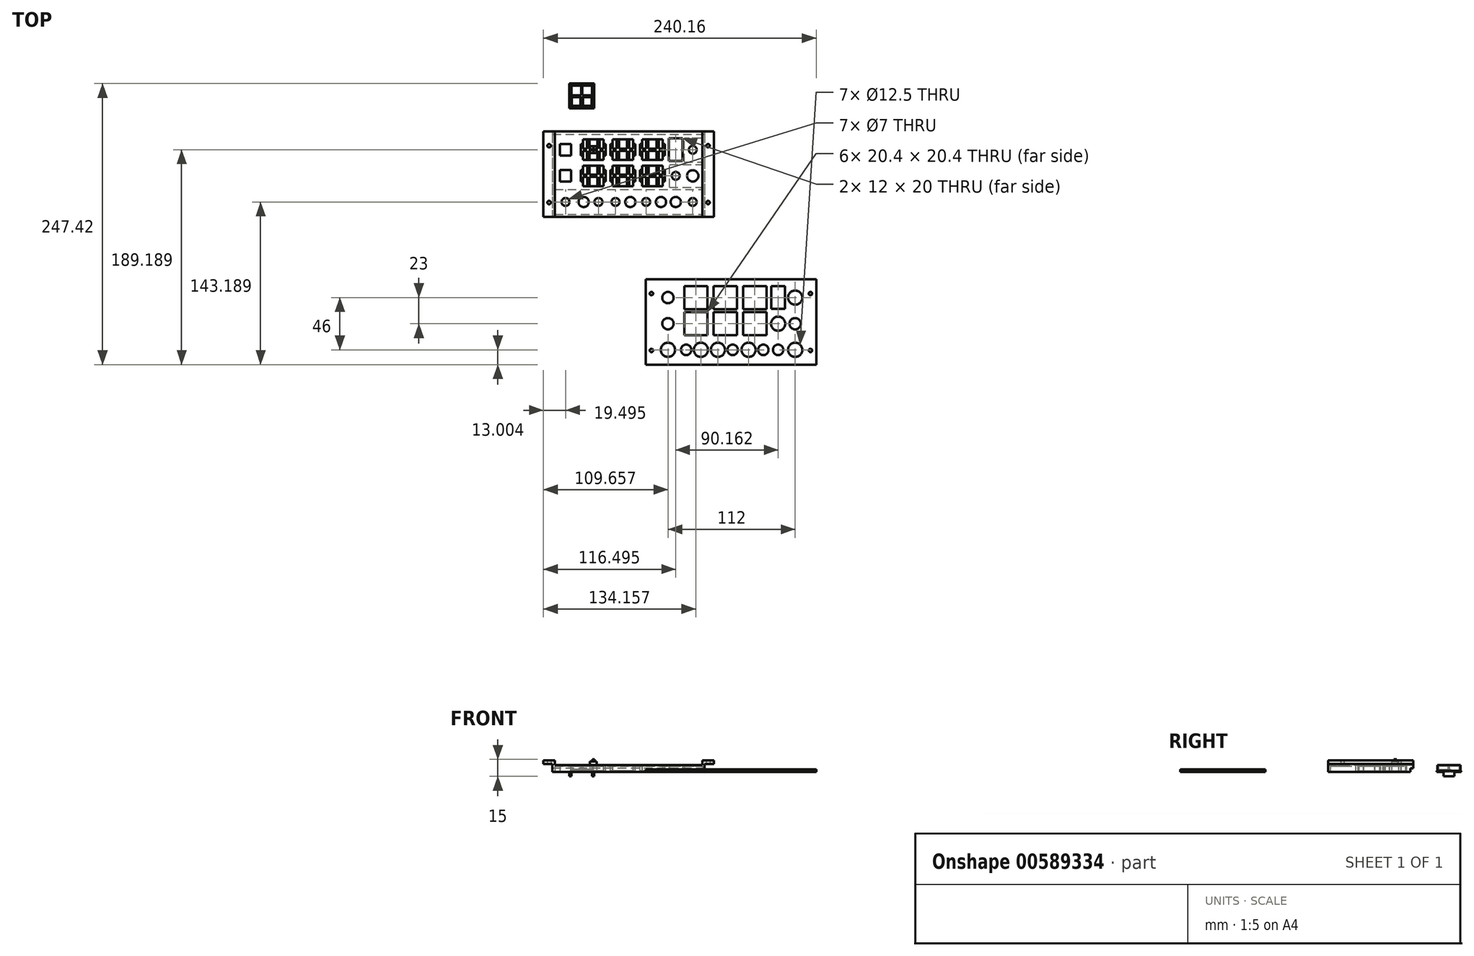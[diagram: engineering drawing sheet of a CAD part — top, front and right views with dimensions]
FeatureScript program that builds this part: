
annotation { "Feature Type Name" : "Feature", "Feature Type Description" : "" }
export const myFeature = defineFeature(function(context is Context, id is Id, definition is map)
    precondition{}
    {
        {
            var Q0;
            Q0=qCreatedBy(makeId("Top.planeOp"),FACE);
            var sketch = newSketch(context, id + "F0", { "sketchPlane" : qUnion([Q0])});
            skLineSegment(sketch, "E0.bottom", {"start": v(-5.5, -57.04) * mm, "end": v(-155.5, -57.04) * mm});
            skLineSegment(sketch, "E0.top", {"start": v(-5.5, 17.96) * mm, "end": v(-155.5, 17.96) * mm});
            skLineSegment(sketch, "E0.left", {"start": v(-5.5, -57.04) * mm, "end": v(-5.5, 17.96) * mm});
            skLineSegment(sketch, "E0.right", {"start": v(-155.5, -57.04) * mm, "end": v(-155.5, 17.96) * mm});
            skPoint(sketch, "E0.middle", {"position": v(-80.5, -19.54) * mm});
            skLineSegment(sketch, "E1.bottom", {"start": v(-101.5, -8.04) * mm, "end": v(-121.5, -8.04) * mm, "construction": true});
            skLineSegment(sketch, "E1.top", {"start": v(-101.5, 11.96) * mm, "end": v(-121.5, 11.96) * mm, "construction": true});
            skLineSegment(sketch, "E1.left", {"start": v(-101.5, -8.04) * mm, "end": v(-101.5, 11.96) * mm, "construction": true});
            skLineSegment(sketch, "E1.right", {"start": v(-121.5, -8.04) * mm, "end": v(-121.5, 11.96) * mm, "construction": true});
            skPoint(sketch, "E1.middle", {"position": v(-111.5, 1.96) * mm});
            skLineSegment(sketch, "E2.1.0.0", {"start": v(-95.5, -8.04) * mm, "end": v(-95.5, 11.96) * mm, "construction": true});
            skPoint(sketch, "E2.1.0.1", {"position": v(-85.5, 1.96) * mm});
            skLineSegment(sketch, "E2.1.0.2", {"start": v(-75.5, -8.04) * mm, "end": v(-95.5, -8.04) * mm, "construction": true});
            skLineSegment(sketch, "E2.1.0.3", {"start": v(-75.5, -8.04) * mm, "end": v(-75.5, 11.96) * mm, "construction": true});
            skLineSegment(sketch, "E2.1.0.4", {"start": v(-75.5, 11.96) * mm, "end": v(-95.5, 11.96) * mm, "construction": true});
            skLineSegment(sketch, "E2.2.0.0", {"start": v(-69.5, -8.04) * mm, "end": v(-69.5, 11.96) * mm, "construction": true});
            skPoint(sketch, "E2.2.0.1", {"position": v(-59.5, 1.96) * mm});
            skLineSegment(sketch, "E2.2.0.2", {"start": v(-49.5, -8.04) * mm, "end": v(-69.5, -8.04) * mm, "construction": true});
            skLineSegment(sketch, "E2.2.0.3", {"start": v(-49.5, -8.04) * mm, "end": v(-49.5, 11.96) * mm, "construction": true});
            skLineSegment(sketch, "E2.2.0.4", {"start": v(-49.5, 11.96) * mm, "end": v(-69.5, 11.96) * mm, "construction": true});
            skLineSegment(sketch, "E2.direction1", {"start": v(-121.5, -8.04) * mm, "end": v(-95.5, -8.04) * mm, "construction": true});
            skLineSegment(sketch, "E3.bottom", {"start": v(-101.5, -31.04) * mm, "end": v(-121.5, -31.04) * mm, "construction": true});
            skLineSegment(sketch, "E3.top", {"start": v(-101.5, -11.04) * mm, "end": v(-121.5, -11.04) * mm, "construction": true});
            skLineSegment(sketch, "E3.left", {"start": v(-101.5, -31.04) * mm, "end": v(-101.5, -11.04) * mm, "construction": true});
            skLineSegment(sketch, "E3.right", {"start": v(-121.5, -31.04) * mm, "end": v(-121.5, -11.04) * mm, "construction": true});
            skPoint(sketch, "E3.middle", {"position": v(-111.5, -21.04) * mm});
            skLineSegment(sketch, "E4.1.0.0", {"start": v(-75.5, -31.04) * mm, "end": v(-95.5, -31.04) * mm, "construction": true});
            skLineSegment(sketch, "E4.1.0.1", {"start": v(-75.5, -31.04) * mm, "end": v(-75.5, -11.04) * mm, "construction": true});
            skLineSegment(sketch, "E4.1.0.2", {"start": v(-95.5, -31.04) * mm, "end": v(-95.5, -11.04) * mm, "construction": true});
            skLineSegment(sketch, "E4.1.0.3", {"start": v(-75.5, -11.04) * mm, "end": v(-95.5, -11.04) * mm, "construction": true});
            skPoint(sketch, "E4.1.0.4", {"position": v(-85.5, -21.04) * mm});
            skLineSegment(sketch, "E4.2.0.0", {"start": v(-49.5, -31.04) * mm, "end": v(-69.5, -31.04) * mm, "construction": true});
            skLineSegment(sketch, "E4.2.0.1", {"start": v(-49.5, -31.04) * mm, "end": v(-49.5, -11.04) * mm, "construction": true});
            skLineSegment(sketch, "E4.2.0.2", {"start": v(-69.5, -31.04) * mm, "end": v(-69.5, -11.04) * mm, "construction": true});
            skLineSegment(sketch, "E4.2.0.3", {"start": v(-49.5, -11.04) * mm, "end": v(-69.5, -11.04) * mm, "construction": true});
            skPoint(sketch, "E4.2.0.4", {"position": v(-59.5, -21.04) * mm});
            skLineSegment(sketch, "E4.direction1", {"start": v(-121.5, -31.04) * mm, "end": v(-95.5, -31.04) * mm, "construction": true});
            skCircle(sketch, "E5", {"center": v(-136, -44.04) * mm, "radius": 3.5 * mm});
            skCircle(sketch, "E6", {"center": v(-107, -44.04) * mm, "radius": 3.5 * mm});
            skCircle(sketch, "E7", {"center": v(-92, -44.04) * mm, "radius": 3.5 * mm});
            skLineSegment(sketch, "E8.bottom", {"start": v(-155.5, 17.96) * mm, "end": v(-147.5, 17.96) * mm, "construction": true});
            skLineSegment(sketch, "E8.top", {"start": v(-155.5, -57.04) * mm, "end": v(-147.5, -57.04) * mm, "construction": true});
            skLineSegment(sketch, "E8.left", {"start": v(-155.5, 17.96) * mm, "end": v(-155.5, -57.04) * mm, "construction": true});
            skLineSegment(sketch, "E8.right", {"start": v(-147.5, 17.96) * mm, "end": v(-147.5, -57.04) * mm, "construction": true});
            skLineSegment(sketch, "E9.bottom", {"start": v(-5.5, -57.04) * mm, "end": v(-13.5, -57.04) * mm, "construction": true});
            skLineSegment(sketch, "E9.top", {"start": v(-5.5, 17.96) * mm, "end": v(-13.5, 17.96) * mm, "construction": true});
            skLineSegment(sketch, "E9.left", {"start": v(-5.5, -57.04) * mm, "end": v(-5.5, 17.96) * mm, "construction": true});
            skLineSegment(sketch, "E9.right", {"start": v(-13.5, -57.04) * mm, "end": v(-13.5, 17.96) * mm, "construction": true});
            skCircle(sketch, "E10", {"center": v(-120, -44.04) * mm, "radius": 4.5 * mm});
            skCircle(sketch, "E11", {"center": v(-79, -44.04) * mm, "radius": 4.5 * mm});
            skCircle(sketch, "E12", {"center": v(-65, -44.04) * mm, "radius": 3.5 * mm});
            skCircle(sketch, "E13", {"center": v(-52, -44.04) * mm, "radius": 4.5 * mm});
            skCircle(sketch, "E14", {"center": v(-39, -44.04) * mm, "radius": 4.5 * mm});
            skCircle(sketch, "E15", {"center": v(-24, -44.04) * mm, "radius": 3.5 * mm});
            skCircle(sketch, "E16", {"center": v(-39, -21.04) * mm, "radius": 3.5 * mm});
            skLineSegment(sketch, "E17.bottom", {"start": v(-33, -8.04) * mm, "end": v(-45, -8.04) * mm});
            skLineSegment(sketch, "E17.top", {"start": v(-33, 11.96) * mm, "end": v(-45, 11.96) * mm});
            skLineSegment(sketch, "E17.left", {"start": v(-33, -8.04) * mm, "end": v(-33, 11.96) * mm});
            skLineSegment(sketch, "E17.right", {"start": v(-45, -8.04) * mm, "end": v(-45, 11.96) * mm});
            skPoint(sketch, "E17.middle", {"position": v(-39, 1.96) * mm});
            skCircle(sketch, "E18", {"center": v(-24, 1.96) * mm, "radius": 3.5 * mm});
            skCircle(sketch, "E19", {"center": v(-24, -21.04) * mm, "radius": 5 * mm});
            skPoint(sketch, "E20.centerSnap0", {"position": v(-121.5, -21.04) * mm});
            skLineSegment(sketch, "E21.bottom", {"start": v(-102.5, -7.04) * mm, "end": v(-120.5, -7.04) * mm});
            skLineSegment(sketch, "E21.top", {"start": v(-102.5, 10.96) * mm, "end": v(-120.5, 10.96) * mm});
            skLineSegment(sketch, "E21.left", {"start": v(-102.5, -7.04) * mm, "end": v(-102.5, 10.96) * mm});
            skLineSegment(sketch, "E21.right", {"start": v(-120.5, -7.04) * mm, "end": v(-120.5, 10.96) * mm});
            skLineSegment(sketch, "E22.bottom", {"start": v(-102.5, -30.04) * mm, "end": v(-120.5, -30.04) * mm});
            skLineSegment(sketch, "E22.top", {"start": v(-102.5, -12.04) * mm, "end": v(-120.5, -12.04) * mm});
            skLineSegment(sketch, "E22.left", {"start": v(-102.5, -30.04) * mm, "end": v(-102.5, -12.04) * mm});
            skLineSegment(sketch, "E22.right", {"start": v(-120.5, -30.04) * mm, "end": v(-120.5, -12.04) * mm});
            skLineSegment(sketch, "E23.bottom", {"start": v(-102.5, 0.96) * mm, "end": v(-106, 0.96) * mm});
            skLineSegment(sketch, "E23.top", {"start": v(-102.5, 2.96) * mm, "end": v(-106, 2.96) * mm});
            skLineSegment(sketch, "E23.left", {"start": v(-102.5, 0.96) * mm, "end": v(-102.5, 2.96) * mm});
            skLineSegment(sketch, "E23.right", {"start": v(-120.5, 0.96) * mm, "end": v(-120.5, 2.96) * mm});
            skLineSegment(sketch, "E24.bottom", {"start": v(-115, -7.04) * mm, "end": v(-117, -7.04) * mm});
            skLineSegment(sketch, "E24.top", {"start": v(-115, 10.96) * mm, "end": v(-117, 10.96) * mm});
            skLineSegment(sketch, "E24.left", {"start": v(-115, -7.04) * mm, "end": v(-115, 0.96) * mm});
            skLineSegment(sketch, "E24.right", {"start": v(-117, -7.04) * mm, "end": v(-117, 0.96) * mm});
            skPoint(sketch, "E24.middle", {"position": v(-116, 1.96) * mm});
            skLineSegment(sketch, "E25.bottom", {"start": v(-106, -7.04) * mm, "end": v(-108, -7.04) * mm});
            skLineSegment(sketch, "E25.top", {"start": v(-106, 10.96) * mm, "end": v(-108, 10.96) * mm});
            skLineSegment(sketch, "E25.left", {"start": v(-106, -7.04) * mm, "end": v(-106, 0.96) * mm});
            skLineSegment(sketch, "E25.right", {"start": v(-108, -7.04) * mm, "end": v(-108, 0.96) * mm});
            skPoint(sketch, "E25.middle", {"position": v(-107, 1.96) * mm});
            skLineSegment(sketch, "E26.trimOffspring", {"start": v(-117, 2.96) * mm, "end": v(-117, 10.96) * mm});
            skLineSegment(sketch, "E27.trimOffspring", {"start": v(-117, 2.96) * mm, "end": v(-120.5, 2.96) * mm});
            skLineSegment(sketch, "E28.trimOffspring", {"start": v(-115, 2.96) * mm, "end": v(-115, 10.96) * mm});
            skLineSegment(sketch, "E29.trimOffspring", {"start": v(-117, 0.96) * mm, "end": v(-120.5, 0.96) * mm});
            skLineSegment(sketch, "E30.trimOffspring", {"start": v(-108, 2.96) * mm, "end": v(-108, 10.96) * mm});
            skLineSegment(sketch, "E31.trimOffspring", {"start": v(-108, 2.96) * mm, "end": v(-115, 2.96) * mm});
            skLineSegment(sketch, "E32.trimOffspring", {"start": v(-106, 2.96) * mm, "end": v(-106, 10.96) * mm});
            skLineSegment(sketch, "E33.trimOffspring", {"start": v(-108, 0.96) * mm, "end": v(-115, 0.96) * mm});
            skLineSegment(sketch, "E34.bottom", {"start": v(-132.5, -50.54) * mm, "end": v(-139.5, -50.54) * mm, "construction": true});
            skLineSegment(sketch, "E34.top", {"start": v(-132.5, -37.54) * mm, "end": v(-139.5, -37.54) * mm, "construction": true});
            skLineSegment(sketch, "E34.left", {"start": v(-132.5, -50.54) * mm, "end": v(-132.5, -37.54) * mm, "construction": true});
            skLineSegment(sketch, "E34.right", {"start": v(-139.5, -50.54) * mm, "end": v(-139.5, -37.54) * mm, "construction": true});
            skLineSegment(sketch, "E35.bottom", {"start": v(-102.5, -22.04) * mm, "end": v(-105.98, -22.04) * mm});
            skLineSegment(sketch, "E35.top", {"start": v(-102.5, -20.04) * mm, "end": v(-105.98, -20.04) * mm});
            skLineSegment(sketch, "E35.left", {"start": v(-102.5, -22.04) * mm, "end": v(-102.5, -20.04) * mm});
            skLineSegment(sketch, "E35.right", {"start": v(-120.5, -22.04) * mm, "end": v(-120.5, -20.04) * mm});
            skLineSegment(sketch, "E36.bottom", {"start": v(-114.98, -30.04) * mm, "end": v(-116.98, -30.04) * mm});
            skLineSegment(sketch, "E36.top", {"start": v(-114.98, -12.04) * mm, "end": v(-116.98, -12.04) * mm});
            skLineSegment(sketch, "E36.left", {"start": v(-114.98, -30.04) * mm, "end": v(-114.98, -22.04) * mm});
            skLineSegment(sketch, "E36.right", {"start": v(-116.98, -30.04) * mm, "end": v(-116.98, -22.04) * mm});
            skPoint(sketch, "E36.middle", {"position": v(-115.98, -21.04) * mm});
            skLineSegment(sketch, "E37.bottom", {"start": v(-105.98, -30.04) * mm, "end": v(-107.98, -30.04) * mm});
            skLineSegment(sketch, "E37.top", {"start": v(-105.98, -12.04) * mm, "end": v(-107.98, -12.04) * mm});
            skLineSegment(sketch, "E37.left", {"start": v(-105.98, -30.04) * mm, "end": v(-105.98, -22.04) * mm});
            skLineSegment(sketch, "E37.right", {"start": v(-107.98, -30.04) * mm, "end": v(-107.98, -22.04) * mm});
            skPoint(sketch, "E37.middle", {"position": v(-106.98, -21.04) * mm});
            skLineSegment(sketch, "E38.trimOffspring", {"start": v(-116.98, -20.04) * mm, "end": v(-116.98, -12.04) * mm});
            skLineSegment(sketch, "E39.trimOffspring", {"start": v(-116.98, -20.04) * mm, "end": v(-120.5, -20.04) * mm});
            skLineSegment(sketch, "E40.trimOffspring", {"start": v(-114.98, -20.04) * mm, "end": v(-114.98, -12.04) * mm});
            skLineSegment(sketch, "E41.trimOffspring", {"start": v(-116.98, -22.04) * mm, "end": v(-120.5, -22.04) * mm});
            skLineSegment(sketch, "E42.trimOffspring", {"start": v(-107.98, -20.04) * mm, "end": v(-107.98, -12.04) * mm});
            skLineSegment(sketch, "E43.trimOffspring", {"start": v(-107.98, -20.04) * mm, "end": v(-114.98, -20.04) * mm});
            skLineSegment(sketch, "E44.trimOffspring", {"start": v(-105.98, -20.04) * mm, "end": v(-105.98, -12.04) * mm});
            skLineSegment(sketch, "E45.trimOffspring", {"start": v(-107.98, -22.04) * mm, "end": v(-114.98, -22.04) * mm});
            skLineSegment(sketch, "E46.bottom", {"start": v(-131, -3.04) * mm, "end": v(-141, -3.04) * mm});
            skLineSegment(sketch, "E46.top", {"start": v(-131, 6.96) * mm, "end": v(-141, 6.96) * mm});
            skLineSegment(sketch, "E46.left", {"start": v(-131, -3.04) * mm, "end": v(-131, 6.96) * mm});
            skLineSegment(sketch, "E46.right", {"start": v(-141, -3.04) * mm, "end": v(-141, 6.96) * mm});
            skPoint(sketch, "E46.middle", {"position": v(-136, 1.96) * mm});
            skLineSegment(sketch, "E47.bottom", {"start": v(-131, -26.04) * mm, "end": v(-141, -26.04) * mm});
            skLineSegment(sketch, "E47.top", {"start": v(-131, -16.04) * mm, "end": v(-141, -16.04) * mm});
            skLineSegment(sketch, "E47.left", {"start": v(-131, -26.04) * mm, "end": v(-131, -16.04) * mm});
            skLineSegment(sketch, "E47.right", {"start": v(-141, -26.04) * mm, "end": v(-141, -16.04) * mm});
            skPoint(sketch, "E47.middle", {"position": v(-136, -21.04) * mm});
            skLineSegment(sketch, "E48.1.0.0", {"start": v(-91, 2.96) * mm, "end": v(-91, 10.96) * mm});
            skLineSegment(sketch, "E48.1.0.2", {"start": v(-76.5, -7.04) * mm, "end": v(-76.5, 10.96) * mm});
            skLineSegment(sketch, "E48.1.0.3", {"start": v(-80, -7.04) * mm, "end": v(-80, 0.96) * mm});
            skPoint(sketch, "E48.1.0.4", {"position": v(-90, 1.96) * mm});
            skLineSegment(sketch, "E48.1.0.5", {"start": v(-82, 2.96) * mm, "end": v(-82, 10.96) * mm});
            skLineSegment(sketch, "E48.1.0.6", {"start": v(-80, 2.96) * mm, "end": v(-80, 10.96) * mm});
            skLineSegment(sketch, "E48.1.0.7", {"start": v(-82, 2.96) * mm, "end": v(-89, 2.96) * mm});
            skLineSegment(sketch, "E48.1.0.8", {"start": v(-76.5, 2.96) * mm, "end": v(-80, 2.96) * mm});
            skLineSegment(sketch, "E48.1.0.9", {"start": v(-76.5, 0.96) * mm, "end": v(-80, 0.96) * mm});
            skLineSegment(sketch, "E48.1.0.10", {"start": v(-80, 10.96) * mm, "end": v(-82, 10.96) * mm});
            skPoint(sketch, "E48.1.0.11", {"position": v(-81, 1.96) * mm});
            skLineSegment(sketch, "E48.1.0.12", {"start": v(-91, 2.96) * mm, "end": v(-94.5, 2.96) * mm});
            skLineSegment(sketch, "E48.1.0.13", {"start": v(-91, 0.96) * mm, "end": v(-94.5, 0.96) * mm});
            skLineSegment(sketch, "E48.1.0.14", {"start": v(-89, 2.96) * mm, "end": v(-89, 10.96) * mm});
            skLineSegment(sketch, "E48.1.0.15", {"start": v(-76.5, 10.96) * mm, "end": v(-94.5, 10.96) * mm});
            skLineSegment(sketch, "E48.1.0.16", {"start": v(-91, -7.04) * mm, "end": v(-91, 0.96) * mm});
            skLineSegment(sketch, "E48.1.0.17", {"start": v(-76.5, -7.04) * mm, "end": v(-94.5, -7.04) * mm});
            skLineSegment(sketch, "E48.1.0.18", {"start": v(-89, -7.04) * mm, "end": v(-89, 0.96) * mm});
            skLineSegment(sketch, "E48.1.0.19", {"start": v(-82, -7.04) * mm, "end": v(-82, 0.96) * mm});
            skLineSegment(sketch, "E48.1.0.20", {"start": v(-94.5, -7.04) * mm, "end": v(-94.5, 10.96) * mm});
            skLineSegment(sketch, "E48.1.0.21", {"start": v(-82, 0.96) * mm, "end": v(-89, 0.96) * mm});
            skLineSegment(sketch, "E48.1.0.22", {"start": v(-80, -7.04) * mm, "end": v(-82, -7.04) * mm});
            skLineSegment(sketch, "E48.1.0.23", {"start": v(-76.5, 0.96) * mm, "end": v(-76.5, 2.96) * mm});
            skLineSegment(sketch, "E48.1.0.24", {"start": v(-89, -7.04) * mm, "end": v(-91, -7.04) * mm});
            skLineSegment(sketch, "E48.1.0.25", {"start": v(-94.5, 0.96) * mm, "end": v(-94.5, 2.96) * mm});
            skLineSegment(sketch, "E48.1.0.27", {"start": v(-89, 10.96) * mm, "end": v(-91, 10.96) * mm});
            skLineSegment(sketch, "E48.2.0.0", {"start": v(-65, 2.96) * mm, "end": v(-65, 10.96) * mm});
            skLineSegment(sketch, "E48.2.0.2", {"start": v(-50.5, -7.04) * mm, "end": v(-50.5, 10.96) * mm});
            skLineSegment(sketch, "E48.2.0.3", {"start": v(-54, -7.04) * mm, "end": v(-54, 0.96) * mm});
            skPoint(sketch, "E48.2.0.4", {"position": v(-64, 1.96) * mm});
            skLineSegment(sketch, "E48.2.0.5", {"start": v(-56, 2.96) * mm, "end": v(-56, 10.96) * mm});
            skLineSegment(sketch, "E48.2.0.6", {"start": v(-54, 2.96) * mm, "end": v(-54, 10.96) * mm});
            skLineSegment(sketch, "E48.2.0.7", {"start": v(-56, 2.96) * mm, "end": v(-63, 2.96) * mm});
            skLineSegment(sketch, "E48.2.0.8", {"start": v(-50.5, 2.96) * mm, "end": v(-54, 2.96) * mm});
            skLineSegment(sketch, "E48.2.0.9", {"start": v(-50.5, 0.96) * mm, "end": v(-54, 0.96) * mm});
            skLineSegment(sketch, "E48.2.0.10", {"start": v(-54, 10.96) * mm, "end": v(-56, 10.96) * mm});
            skPoint(sketch, "E48.2.0.11", {"position": v(-55, 1.96) * mm});
            skLineSegment(sketch, "E48.2.0.12", {"start": v(-65, 2.96) * mm, "end": v(-68.5, 2.96) * mm});
            skLineSegment(sketch, "E48.2.0.13", {"start": v(-65, 0.96) * mm, "end": v(-68.5, 0.96) * mm});
            skLineSegment(sketch, "E48.2.0.14", {"start": v(-63, 2.96) * mm, "end": v(-63, 10.96) * mm});
            skLineSegment(sketch, "E48.2.0.15", {"start": v(-50.5, 10.96) * mm, "end": v(-68.5, 10.96) * mm});
            skLineSegment(sketch, "E48.2.0.16", {"start": v(-65, -7.04) * mm, "end": v(-65, 0.96) * mm});
            skLineSegment(sketch, "E48.2.0.17", {"start": v(-50.5, -7.04) * mm, "end": v(-68.5, -7.04) * mm});
            skLineSegment(sketch, "E48.2.0.18", {"start": v(-63, -7.04) * mm, "end": v(-63, 0.96) * mm});
            skLineSegment(sketch, "E48.2.0.19", {"start": v(-56, -7.04) * mm, "end": v(-56, 0.96) * mm});
            skLineSegment(sketch, "E48.2.0.20", {"start": v(-68.5, -7.04) * mm, "end": v(-68.5, 10.96) * mm});
            skLineSegment(sketch, "E48.2.0.21", {"start": v(-56, 0.96) * mm, "end": v(-63, 0.96) * mm});
            skLineSegment(sketch, "E48.2.0.22", {"start": v(-54, -7.04) * mm, "end": v(-56, -7.04) * mm});
            skLineSegment(sketch, "E48.2.0.23", {"start": v(-50.5, 0.96) * mm, "end": v(-50.5, 2.96) * mm});
            skLineSegment(sketch, "E48.2.0.24", {"start": v(-63, -7.04) * mm, "end": v(-65, -7.04) * mm});
            skLineSegment(sketch, "E48.2.0.25", {"start": v(-68.5, 0.96) * mm, "end": v(-68.5, 2.96) * mm});
            skLineSegment(sketch, "E48.2.0.27", {"start": v(-63, 10.96) * mm, "end": v(-65, 10.96) * mm});
            skLineSegment(sketch, "E48.direction1", {"start": v(-120.5, -7.04) * mm, "end": v(-94.5, -7.04) * mm, "construction": true});
            skLineSegment(sketch, "E49.1.0.0", {"start": v(-76.5, -20.04) * mm, "end": v(-79.98, -20.04) * mm});
            skLineSegment(sketch, "E49.1.0.1", {"start": v(-88.98, -20.04) * mm, "end": v(-88.98, -12.04) * mm});
            skLineSegment(sketch, "E49.1.0.2", {"start": v(-81.98, -30.04) * mm, "end": v(-81.98, -22.04) * mm});
            skLineSegment(sketch, "E49.1.0.3", {"start": v(-94.5, -30.04) * mm, "end": v(-94.5, -12.04) * mm});
            skLineSegment(sketch, "E49.1.0.4", {"start": v(-90.98, -30.04) * mm, "end": v(-90.98, -22.04) * mm});
            skLineSegment(sketch, "E49.1.0.5", {"start": v(-76.5, -30.04) * mm, "end": v(-76.5, -12.04) * mm});
            skLineSegment(sketch, "E49.1.0.6", {"start": v(-81.98, -22.04) * mm, "end": v(-88.98, -22.04) * mm});
            skLineSegment(sketch, "E49.1.0.7", {"start": v(-88.98, -30.04) * mm, "end": v(-88.98, -22.04) * mm});
            skLineSegment(sketch, "E49.1.0.9", {"start": v(-79.98, -20.04) * mm, "end": v(-79.98, -12.04) * mm});
            skLineSegment(sketch, "E49.1.0.10", {"start": v(-76.5, -22.04) * mm, "end": v(-79.98, -22.04) * mm});
            skPoint(sketch, "E49.1.0.11", {"position": v(-80.98, -21.04) * mm});
            skLineSegment(sketch, "E49.1.0.12", {"start": v(-90.98, -22.04) * mm, "end": v(-94.5, -22.04) * mm});
            skLineSegment(sketch, "E49.1.0.14", {"start": v(-81.98, -20.04) * mm, "end": v(-88.98, -20.04) * mm});
            skPoint(sketch, "E49.1.0.15", {"position": v(-89.98, -21.04) * mm});
            skLineSegment(sketch, "E49.1.0.16", {"start": v(-79.98, -30.04) * mm, "end": v(-79.98, -22.04) * mm});
            skLineSegment(sketch, "E49.1.0.17", {"start": v(-76.5, -30.04) * mm, "end": v(-94.5, -30.04) * mm});
            skLineSegment(sketch, "E49.1.0.18", {"start": v(-90.98, -20.04) * mm, "end": v(-90.98, -12.04) * mm});
            skLineSegment(sketch, "E49.1.0.19", {"start": v(-81.98, -20.04) * mm, "end": v(-81.98, -12.04) * mm});
            skLineSegment(sketch, "E49.1.0.20", {"start": v(-90.98, -20.04) * mm, "end": v(-94.5, -20.04) * mm});
            skLineSegment(sketch, "E49.1.0.21", {"start": v(-76.5, -12.04) * mm, "end": v(-94.5, -12.04) * mm});
            skLineSegment(sketch, "E49.1.0.22", {"start": v(-88.98, -12.04) * mm, "end": v(-90.98, -12.04) * mm});
            skLineSegment(sketch, "E49.1.0.23", {"start": v(-76.5, -22.04) * mm, "end": v(-76.5, -20.04) * mm});
            skLineSegment(sketch, "E49.1.0.24", {"start": v(-94.5, -22.04) * mm, "end": v(-94.5, -20.04) * mm});
            skLineSegment(sketch, "E49.1.0.26", {"start": v(-94.5, -30.04) * mm, "end": v(-94.5, -12.04) * mm});
            skLineSegment(sketch, "E49.1.0.27", {"start": v(-79.98, -12.04) * mm, "end": v(-81.98, -12.04) * mm});
            skLineSegment(sketch, "E49.1.0.28", {"start": v(-76.5, -30.04) * mm, "end": v(-94.5, -30.04) * mm});
            skLineSegment(sketch, "E49.1.0.29", {"start": v(-76.5, -12.04) * mm, "end": v(-94.5, -12.04) * mm});
            skLineSegment(sketch, "E49.1.0.30", {"start": v(-76.5, -30.04) * mm, "end": v(-76.5, -12.04) * mm});
            skLineSegment(sketch, "E49.1.0.31", {"start": v(-88.98, -30.04) * mm, "end": v(-90.98, -30.04) * mm});
            skLineSegment(sketch, "E49.1.0.32", {"start": v(-79.98, -30.04) * mm, "end": v(-81.98, -30.04) * mm});
            skLineSegment(sketch, "E49.2.0.0", {"start": v(-50.5, -20.04) * mm, "end": v(-53.98, -20.04) * mm});
            skLineSegment(sketch, "E49.2.0.1", {"start": v(-62.98, -20.04) * mm, "end": v(-62.98, -12.04) * mm});
            skLineSegment(sketch, "E49.2.0.2", {"start": v(-55.98, -30.04) * mm, "end": v(-55.98, -22.04) * mm});
            skLineSegment(sketch, "E49.2.0.3", {"start": v(-68.5, -30.04) * mm, "end": v(-68.5, -12.04) * mm});
            skLineSegment(sketch, "E49.2.0.4", {"start": v(-64.98, -30.04) * mm, "end": v(-64.98, -22.04) * mm});
            skLineSegment(sketch, "E49.2.0.5", {"start": v(-50.5, -30.04) * mm, "end": v(-50.5, -12.04) * mm});
            skLineSegment(sketch, "E49.2.0.6", {"start": v(-55.98, -22.04) * mm, "end": v(-62.98, -22.04) * mm});
            skLineSegment(sketch, "E49.2.0.7", {"start": v(-62.98, -30.04) * mm, "end": v(-62.98, -22.04) * mm});
            skLineSegment(sketch, "E49.2.0.9", {"start": v(-53.98, -20.04) * mm, "end": v(-53.98, -12.04) * mm});
            skLineSegment(sketch, "E49.2.0.10", {"start": v(-50.5, -22.04) * mm, "end": v(-53.98, -22.04) * mm});
            skPoint(sketch, "E49.2.0.11", {"position": v(-54.98, -21.04) * mm});
            skLineSegment(sketch, "E49.2.0.12", {"start": v(-64.98, -22.04) * mm, "end": v(-68.5, -22.04) * mm});
            skLineSegment(sketch, "E49.2.0.14", {"start": v(-55.98, -20.04) * mm, "end": v(-62.98, -20.04) * mm});
            skPoint(sketch, "E49.2.0.15", {"position": v(-63.98, -21.04) * mm});
            skLineSegment(sketch, "E49.2.0.16", {"start": v(-53.98, -30.04) * mm, "end": v(-53.98, -22.04) * mm});
            skLineSegment(sketch, "E49.2.0.17", {"start": v(-50.5, -30.04) * mm, "end": v(-68.5, -30.04) * mm});
            skLineSegment(sketch, "E49.2.0.18", {"start": v(-64.98, -20.04) * mm, "end": v(-64.98, -12.04) * mm});
            skLineSegment(sketch, "E49.2.0.19", {"start": v(-55.98, -20.04) * mm, "end": v(-55.98, -12.04) * mm});
            skLineSegment(sketch, "E49.2.0.20", {"start": v(-64.98, -20.04) * mm, "end": v(-68.5, -20.04) * mm});
            skLineSegment(sketch, "E49.2.0.21", {"start": v(-50.5, -12.04) * mm, "end": v(-68.5, -12.04) * mm});
            skLineSegment(sketch, "E49.2.0.22", {"start": v(-62.98, -12.04) * mm, "end": v(-64.98, -12.04) * mm});
            skLineSegment(sketch, "E49.2.0.23", {"start": v(-50.5, -22.04) * mm, "end": v(-50.5, -20.04) * mm});
            skLineSegment(sketch, "E49.2.0.24", {"start": v(-68.5, -22.04) * mm, "end": v(-68.5, -20.04) * mm});
            skLineSegment(sketch, "E49.2.0.26", {"start": v(-68.5, -30.04) * mm, "end": v(-68.5, -12.04) * mm});
            skLineSegment(sketch, "E49.2.0.27", {"start": v(-53.98, -12.04) * mm, "end": v(-55.98, -12.04) * mm});
            skLineSegment(sketch, "E49.2.0.28", {"start": v(-50.5, -30.04) * mm, "end": v(-68.5, -30.04) * mm});
            skLineSegment(sketch, "E49.2.0.29", {"start": v(-50.5, -12.04) * mm, "end": v(-68.5, -12.04) * mm});
            skLineSegment(sketch, "E49.2.0.30", {"start": v(-50.5, -30.04) * mm, "end": v(-50.5, -12.04) * mm});
            skLineSegment(sketch, "E49.2.0.31", {"start": v(-62.98, -30.04) * mm, "end": v(-64.98, -30.04) * mm});
            skLineSegment(sketch, "E49.2.0.32", {"start": v(-53.98, -30.04) * mm, "end": v(-55.98, -30.04) * mm});
            skLineSegment(sketch, "E49.direction1", {"start": v(-120.5, -30.04) * mm, "end": v(-94.5, -30.04) * mm, "construction": true});
            skLineSegment(sketch, "E50.bottom", {"start": v(-135, -3.04) * mm, "end": v(-137, -3.04) * mm});
            skLineSegment(sketch, "E50.top", {"start": v(-135, 6.96) * mm, "end": v(-137, 6.96) * mm});
            skLineSegment(sketch, "E50.left", {"start": v(-135, -3.04) * mm, "end": v(-135, 6.96) * mm});
            skLineSegment(sketch, "E50.right", {"start": v(-137, -3.04) * mm, "end": v(-137, 6.96) * mm});
            skLineSegment(sketch, "E51.bottom", {"start": v(-135, -26.04) * mm, "end": v(-137, -26.04) * mm});
            skLineSegment(sketch, "E51.top", {"start": v(-135, -16.04) * mm, "end": v(-137, -16.04) * mm});
            skLineSegment(sketch, "E51.left", {"start": v(-135, -26.04) * mm, "end": v(-135, -16.04) * mm});
            skLineSegment(sketch, "E51.right", {"start": v(-137, -26.04) * mm, "end": v(-137, -16.04) * mm});
            skCircle(sketch, "E52", {"center": v(-150.5, 5.46) * mm, "radius": 1.5 * mm});
            skPoint(sketch, "E52.centerSnap0", {"position": v(-151.5, 17.96) * mm});
            skCircle(sketch, "E53", {"center": v(-150.5, -44.54) * mm, "radius": 1.5 * mm});
            skCircle(sketch, "E54", {"center": v(-10.5, 5.46) * mm, "radius": 1.5 * mm});
            skCircle(sketch, "E55", {"center": v(-10.5, -44.54) * mm, "radius": 1.5 * mm});
            skSolve(sketch);
        }
        {
            var Q0;
            Q0=qCreatedBy(makeId("Top.planeOp"),FACE);
            var sketch = newSketch(context, id + "F1", { "sketchPlane" : qUnion([Q0])});
            skLineSegment(sketch, "E56.bottom", {"start": v(84.66, -187.23) * mm, "end": v(-65.34, -187.23) * mm});
            skLineSegment(sketch, "E56.top", {"start": v(84.66, -112.23) * mm, "end": v(-65.34, -112.23) * mm});
            skLineSegment(sketch, "E56.left", {"start": v(84.66, -187.23) * mm, "end": v(84.66, -112.23) * mm});
            skLineSegment(sketch, "E56.right", {"start": v(-65.34, -187.23) * mm, "end": v(-65.34, -112.23) * mm});
            skPoint(sketch, "E56.middle", {"position": v(9.66, -149.73) * mm});
            skLineSegment(sketch, "E57.bottom", {"start": v(-11.14, -138.43) * mm, "end": v(-31.54, -138.43) * mm});
            skLineSegment(sketch, "E57.top", {"start": v(-11.14, -118.03) * mm, "end": v(-31.54, -118.03) * mm});
            skLineSegment(sketch, "E57.left", {"start": v(-11.14, -138.43) * mm, "end": v(-11.14, -118.03) * mm});
            skLineSegment(sketch, "E57.right", {"start": v(-31.54, -138.43) * mm, "end": v(-31.54, -118.03) * mm});
            skPoint(sketch, "E57.middle", {"position": v(-21.34, -128.23) * mm});
            skLineSegment(sketch, "E58.1.0.0", {"start": v(-5.54, -138.43) * mm, "end": v(-5.54, -118.03) * mm});
            skPoint(sketch, "E58.1.0.1", {"position": v(4.66, -128.23) * mm});
            skLineSegment(sketch, "E58.1.0.2", {"start": v(14.86, -138.43) * mm, "end": v(-5.54, -138.43) * mm});
            skLineSegment(sketch, "E58.1.0.3", {"start": v(14.86, -138.43) * mm, "end": v(14.86, -118.03) * mm});
            skLineSegment(sketch, "E58.1.0.4", {"start": v(14.86, -118.03) * mm, "end": v(-5.54, -118.03) * mm});
            skLineSegment(sketch, "E58.2.0.0", {"start": v(20.46, -138.43) * mm, "end": v(20.46, -118.03) * mm});
            skPoint(sketch, "E58.2.0.1", {"position": v(30.66, -128.23) * mm});
            skLineSegment(sketch, "E58.2.0.2", {"start": v(40.86, -138.43) * mm, "end": v(20.46, -138.43) * mm});
            skLineSegment(sketch, "E58.2.0.3", {"start": v(40.86, -138.43) * mm, "end": v(40.86, -118.03) * mm});
            skLineSegment(sketch, "E58.2.0.4", {"start": v(40.86, -118.03) * mm, "end": v(20.46, -118.03) * mm});
            skLineSegment(sketch, "E58.direction1", {"start": v(-31.54, -138.43) * mm, "end": v(-5.54, -138.43) * mm, "construction": true});
            skLineSegment(sketch, "E59.bottom", {"start": v(-11.14, -161.43) * mm, "end": v(-31.54, -161.43) * mm});
            skLineSegment(sketch, "E59.top", {"start": v(-11.14, -141.03) * mm, "end": v(-31.54, -141.03) * mm});
            skLineSegment(sketch, "E59.left", {"start": v(-11.14, -161.43) * mm, "end": v(-11.14, -141.03) * mm});
            skLineSegment(sketch, "E59.right", {"start": v(-31.54, -161.43) * mm, "end": v(-31.54, -141.03) * mm});
            skPoint(sketch, "E59.middle", {"position": v(-21.34, -151.23) * mm});
            skLineSegment(sketch, "E60.1.0.0", {"start": v(14.86, -161.43) * mm, "end": v(-5.54, -161.43) * mm});
            skLineSegment(sketch, "E60.1.0.1", {"start": v(14.86, -161.43) * mm, "end": v(14.86, -141.03) * mm});
            skLineSegment(sketch, "E60.1.0.2", {"start": v(-5.54, -161.43) * mm, "end": v(-5.54, -141.03) * mm});
            skLineSegment(sketch, "E60.1.0.3", {"start": v(14.86, -141.03) * mm, "end": v(-5.54, -141.03) * mm});
            skPoint(sketch, "E60.1.0.4", {"position": v(4.66, -151.23) * mm});
            skLineSegment(sketch, "E60.2.0.0", {"start": v(40.86, -161.43) * mm, "end": v(20.46, -161.43) * mm});
            skLineSegment(sketch, "E60.2.0.1", {"start": v(40.86, -161.43) * mm, "end": v(40.86, -141.03) * mm});
            skLineSegment(sketch, "E60.2.0.2", {"start": v(20.46, -161.43) * mm, "end": v(20.46, -141.03) * mm});
            skLineSegment(sketch, "E60.2.0.3", {"start": v(40.86, -141.03) * mm, "end": v(20.46, -141.03) * mm});
            skPoint(sketch, "E60.2.0.4", {"position": v(30.66, -151.23) * mm});
            skLineSegment(sketch, "E60.direction1", {"start": v(-31.54, -161.43) * mm, "end": v(-5.54, -161.43) * mm, "construction": true});
            skCircle(sketch, "E61", {"center": v(-45.84, -174.23) * mm, "radius": 3.5 * mm, "construction": true});
            skCircle(sketch, "E62", {"center": v(-16.84, -174.23) * mm, "radius": 3.5 * mm, "construction": true});
            skCircle(sketch, "E63", {"center": v(-1.84, -174.23) * mm, "radius": 3.5 * mm, "construction": true});
            skLineSegment(sketch, "E64.bottom", {"start": v(-65.34, -112.23) * mm, "end": v(-57.34, -112.23) * mm, "construction": true});
            skLineSegment(sketch, "E64.top", {"start": v(-65.34, -187.23) * mm, "end": v(-57.34, -187.23) * mm, "construction": true});
            skLineSegment(sketch, "E64.left", {"start": v(-65.34, -112.23) * mm, "end": v(-65.34, -187.23) * mm, "construction": true});
            skLineSegment(sketch, "E64.right", {"start": v(-57.34, -112.23) * mm, "end": v(-57.34, -187.23) * mm, "construction": true});
            skLineSegment(sketch, "E65.bottom", {"start": v(84.66, -187.23) * mm, "end": v(76.66, -187.23) * mm, "construction": true});
            skLineSegment(sketch, "E65.top", {"start": v(84.66, -112.23) * mm, "end": v(76.66, -112.23) * mm, "construction": true});
            skLineSegment(sketch, "E65.left", {"start": v(84.66, -187.23) * mm, "end": v(84.66, -112.23) * mm, "construction": true});
            skLineSegment(sketch, "E65.right", {"start": v(76.66, -187.23) * mm, "end": v(76.66, -112.23) * mm, "construction": true});
            skCircle(sketch, "E66", {"center": v(-29.84, -174.23) * mm, "radius": 4.6 * mm});
            skCircle(sketch, "E67", {"center": v(11.16, -174.23) * mm, "radius": 4.6 * mm});
            skCircle(sketch, "E68", {"center": v(25.16, -174.23) * mm, "radius": 3.5 * mm, "construction": true});
            skCircle(sketch, "E69", {"center": v(38.16, -174.23) * mm, "radius": 4.6 * mm});
            skCircle(sketch, "E70", {"center": v(51.16, -174.23) * mm, "radius": 4.6 * mm});
            skCircle(sketch, "E71", {"center": v(66.16, -174.23) * mm, "radius": 3.5 * mm, "construction": true});
            skCircle(sketch, "E72", {"center": v(51.16, -151.23) * mm, "radius": 3.5 * mm, "construction": true});
            skLineSegment(sketch, "E73.bottom", {"start": v(57.16, -138.23) * mm, "end": v(45.16, -138.23) * mm});
            skLineSegment(sketch, "E73.top", {"start": v(57.16, -118.23) * mm, "end": v(45.16, -118.23) * mm});
            skLineSegment(sketch, "E73.left", {"start": v(57.16, -138.23) * mm, "end": v(57.16, -118.23) * mm});
            skLineSegment(sketch, "E73.right", {"start": v(45.16, -138.23) * mm, "end": v(45.16, -118.23) * mm});
            skPoint(sketch, "E73.middle", {"position": v(51.16, -128.23) * mm});
            skCircle(sketch, "E74", {"center": v(66.16, -128.23) * mm, "radius": 3.5 * mm, "construction": true});
            skCircle(sketch, "E75", {"center": v(66.16, -151.23) * mm, "radius": 5 * mm});
            skPoint(sketch, "E76.centerSnap0", {"position": v(-31.54, -151.23) * mm});
            skLineSegment(sketch, "E77.bottom", {"start": v(-12.34, -137.23) * mm, "end": v(-30.34, -137.23) * mm, "construction": true});
            skLineSegment(sketch, "E77.top", {"start": v(-12.34, -119.23) * mm, "end": v(-30.34, -119.23) * mm, "construction": true});
            skLineSegment(sketch, "E77.left", {"start": v(-12.34, -137.23) * mm, "end": v(-12.34, -119.23) * mm, "construction": true});
            skLineSegment(sketch, "E77.right", {"start": v(-30.34, -137.23) * mm, "end": v(-30.34, -119.23) * mm, "construction": true});
            skLineSegment(sketch, "E78.bottom", {"start": v(-12.34, -160.23) * mm, "end": v(-30.34, -160.23) * mm, "construction": true});
            skLineSegment(sketch, "E78.top", {"start": v(-12.34, -142.23) * mm, "end": v(-30.34, -142.23) * mm, "construction": true});
            skLineSegment(sketch, "E78.left", {"start": v(-12.34, -160.23) * mm, "end": v(-12.34, -142.23) * mm, "construction": true});
            skLineSegment(sketch, "E78.right", {"start": v(-30.34, -160.23) * mm, "end": v(-30.34, -142.23) * mm, "construction": true});
            skLineSegment(sketch, "E79.bottom", {"start": v(-12.34, -129.23) * mm, "end": v(-15.84, -129.23) * mm, "construction": true});
            skLineSegment(sketch, "E79.top", {"start": v(-12.34, -127.23) * mm, "end": v(-15.84, -127.23) * mm, "construction": true});
            skLineSegment(sketch, "E79.left", {"start": v(-12.34, -129.23) * mm, "end": v(-12.34, -127.23) * mm, "construction": true});
            skLineSegment(sketch, "E79.right", {"start": v(-30.34, -129.23) * mm, "end": v(-30.34, -127.23) * mm, "construction": true});
            skLineSegment(sketch, "E80.bottom", {"start": v(-24.84, -137.23) * mm, "end": v(-26.84, -137.23) * mm, "construction": true});
            skLineSegment(sketch, "E80.top", {"start": v(-24.84, -119.23) * mm, "end": v(-26.84, -119.23) * mm, "construction": true});
            skLineSegment(sketch, "E80.left", {"start": v(-24.84, -137.23) * mm, "end": v(-24.84, -129.23) * mm, "construction": true});
            skLineSegment(sketch, "E80.right", {"start": v(-26.84, -137.23) * mm, "end": v(-26.84, -129.23) * mm, "construction": true});
            skPoint(sketch, "E80.middle", {"position": v(-25.84, -128.23) * mm});
            skLineSegment(sketch, "E81.bottom", {"start": v(-15.84, -137.23) * mm, "end": v(-17.84, -137.23) * mm, "construction": true});
            skLineSegment(sketch, "E81.top", {"start": v(-15.84, -119.23) * mm, "end": v(-17.84, -119.23) * mm, "construction": true});
            skLineSegment(sketch, "E81.left", {"start": v(-15.84, -137.23) * mm, "end": v(-15.84, -129.23) * mm, "construction": true});
            skLineSegment(sketch, "E81.right", {"start": v(-17.84, -137.23) * mm, "end": v(-17.84, -129.23) * mm, "construction": true});
            skPoint(sketch, "E81.middle", {"position": v(-16.84, -128.23) * mm});
            skLineSegment(sketch, "E82.trimOffspring", {"start": v(-26.84, -127.23) * mm, "end": v(-26.84, -119.23) * mm, "construction": true});
            skLineSegment(sketch, "E83.trimOffspring", {"start": v(-26.84, -127.23) * mm, "end": v(-30.34, -127.23) * mm, "construction": true});
            skLineSegment(sketch, "E84.trimOffspring", {"start": v(-24.84, -127.23) * mm, "end": v(-24.84, -119.23) * mm, "construction": true});
            skLineSegment(sketch, "E85.trimOffspring", {"start": v(-26.84, -129.23) * mm, "end": v(-30.34, -129.23) * mm, "construction": true});
            skLineSegment(sketch, "E86.trimOffspring", {"start": v(-17.84, -127.23) * mm, "end": v(-17.84, -119.23) * mm, "construction": true});
            skLineSegment(sketch, "E87.trimOffspring", {"start": v(-17.84, -127.23) * mm, "end": v(-24.84, -127.23) * mm, "construction": true});
            skLineSegment(sketch, "E88.trimOffspring", {"start": v(-15.84, -127.23) * mm, "end": v(-15.84, -119.23) * mm, "construction": true});
            skLineSegment(sketch, "E89.trimOffspring", {"start": v(-17.84, -129.23) * mm, "end": v(-24.84, -129.23) * mm, "construction": true});
            skLineSegment(sketch, "E90.bottom", {"start": v(-42.34, -180.73) * mm, "end": v(-49.34, -180.73) * mm, "construction": true});
            skLineSegment(sketch, "E90.top", {"start": v(-42.34, -167.73) * mm, "end": v(-49.34, -167.73) * mm, "construction": true});
            skLineSegment(sketch, "E90.left", {"start": v(-42.34, -180.73) * mm, "end": v(-42.34, -167.73) * mm, "construction": true});
            skLineSegment(sketch, "E90.right", {"start": v(-49.34, -180.73) * mm, "end": v(-49.34, -167.73) * mm, "construction": true});
            skLineSegment(sketch, "E91.bottom", {"start": v(-12.34, -152.23) * mm, "end": v(-15.82, -152.23) * mm, "construction": true});
            skLineSegment(sketch, "E91.top", {"start": v(-12.34, -150.23) * mm, "end": v(-15.82, -150.23) * mm, "construction": true});
            skLineSegment(sketch, "E91.left", {"start": v(-12.34, -152.23) * mm, "end": v(-12.34, -150.23) * mm, "construction": true});
            skLineSegment(sketch, "E91.right", {"start": v(-30.34, -152.23) * mm, "end": v(-30.34, -150.23) * mm, "construction": true});
            skLineSegment(sketch, "E92.bottom", {"start": v(-24.82, -160.23) * mm, "end": v(-26.82, -160.23) * mm, "construction": true});
            skLineSegment(sketch, "E92.top", {"start": v(-24.82, -142.23) * mm, "end": v(-26.82, -142.23) * mm, "construction": true});
            skLineSegment(sketch, "E92.left", {"start": v(-24.82, -160.23) * mm, "end": v(-24.82, -152.23) * mm, "construction": true});
            skLineSegment(sketch, "E92.right", {"start": v(-26.82, -160.23) * mm, "end": v(-26.82, -152.23) * mm, "construction": true});
            skPoint(sketch, "E92.middle", {"position": v(-25.82, -151.23) * mm});
            skLineSegment(sketch, "E93.bottom", {"start": v(-15.82, -160.23) * mm, "end": v(-17.82, -160.23) * mm, "construction": true});
            skLineSegment(sketch, "E93.top", {"start": v(-15.82, -142.23) * mm, "end": v(-17.82, -142.23) * mm, "construction": true});
            skLineSegment(sketch, "E93.left", {"start": v(-15.82, -160.23) * mm, "end": v(-15.82, -152.23) * mm, "construction": true});
            skLineSegment(sketch, "E93.right", {"start": v(-17.82, -160.23) * mm, "end": v(-17.82, -152.23) * mm, "construction": true});
            skPoint(sketch, "E93.middle", {"position": v(-16.82, -151.23) * mm});
            skLineSegment(sketch, "E94.trimOffspring", {"start": v(-26.82, -150.23) * mm, "end": v(-26.82, -142.23) * mm, "construction": true});
            skLineSegment(sketch, "E95.trimOffspring", {"start": v(-26.82, -150.23) * mm, "end": v(-30.34, -150.23) * mm, "construction": true});
            skLineSegment(sketch, "E96.trimOffspring", {"start": v(-24.82, -150.23) * mm, "end": v(-24.82, -142.23) * mm, "construction": true});
            skLineSegment(sketch, "E97.trimOffspring", {"start": v(-26.82, -152.23) * mm, "end": v(-30.34, -152.23) * mm, "construction": true});
            skLineSegment(sketch, "E98.trimOffspring", {"start": v(-17.82, -150.23) * mm, "end": v(-17.82, -142.23) * mm, "construction": true});
            skLineSegment(sketch, "E99.trimOffspring", {"start": v(-17.82, -150.23) * mm, "end": v(-24.82, -150.23) * mm, "construction": true});
            skLineSegment(sketch, "E100.trimOffspring", {"start": v(-15.82, -150.23) * mm, "end": v(-15.82, -142.23) * mm, "construction": true});
            skLineSegment(sketch, "E101.trimOffspring", {"start": v(-17.82, -152.23) * mm, "end": v(-24.82, -152.23) * mm, "construction": true});
            skLineSegment(sketch, "E102.bottom", {"start": v(-40.84, -133.23) * mm, "end": v(-50.84, -133.23) * mm, "construction": true});
            skLineSegment(sketch, "E102.top", {"start": v(-40.84, -123.23) * mm, "end": v(-50.84, -123.23) * mm, "construction": true});
            skLineSegment(sketch, "E102.left", {"start": v(-40.84, -133.23) * mm, "end": v(-40.84, -123.23) * mm, "construction": true});
            skLineSegment(sketch, "E102.right", {"start": v(-50.84, -133.23) * mm, "end": v(-50.84, -123.23) * mm, "construction": true});
            skPoint(sketch, "E102.middle", {"position": v(-45.84, -128.23) * mm});
            skLineSegment(sketch, "E103.bottom", {"start": v(-40.84, -156.23) * mm, "end": v(-50.84, -156.23) * mm, "construction": true});
            skLineSegment(sketch, "E103.top", {"start": v(-40.84, -146.23) * mm, "end": v(-50.84, -146.23) * mm, "construction": true});
            skLineSegment(sketch, "E103.left", {"start": v(-40.84, -156.23) * mm, "end": v(-40.84, -146.23) * mm, "construction": true});
            skLineSegment(sketch, "E103.right", {"start": v(-50.84, -156.23) * mm, "end": v(-50.84, -146.23) * mm, "construction": true});
            skPoint(sketch, "E103.middle", {"position": v(-45.84, -151.23) * mm});
            skLineSegment(sketch, "E104.1.0.0", {"start": v(-0.84, -127.23) * mm, "end": v(-0.84, -119.23) * mm, "construction": true});
            skLineSegment(sketch, "E104.1.0.2", {"start": v(13.66, -137.23) * mm, "end": v(13.66, -119.23) * mm, "construction": true});
            skLineSegment(sketch, "E104.1.0.3", {"start": v(10.16, -137.23) * mm, "end": v(10.16, -129.23) * mm, "construction": true});
            skPoint(sketch, "E104.1.0.4", {"position": v(0.16, -128.23) * mm});
            skLineSegment(sketch, "E104.1.0.5", {"start": v(8.16, -127.23) * mm, "end": v(8.16, -119.23) * mm, "construction": true});
            skLineSegment(sketch, "E104.1.0.6", {"start": v(10.16, -127.23) * mm, "end": v(10.16, -119.23) * mm, "construction": true});
            skLineSegment(sketch, "E104.1.0.7", {"start": v(8.16, -127.23) * mm, "end": v(1.16, -127.23) * mm, "construction": true});
            skLineSegment(sketch, "E104.1.0.8", {"start": v(13.66, -127.23) * mm, "end": v(10.16, -127.23) * mm, "construction": true});
            skLineSegment(sketch, "E104.1.0.9", {"start": v(13.66, -129.23) * mm, "end": v(10.16, -129.23) * mm, "construction": true});
            skLineSegment(sketch, "E104.1.0.10", {"start": v(10.16, -119.23) * mm, "end": v(8.16, -119.23) * mm, "construction": true});
            skPoint(sketch, "E104.1.0.11", {"position": v(9.16, -128.23) * mm});
            skLineSegment(sketch, "E104.1.0.12", {"start": v(-0.84, -127.23) * mm, "end": v(-4.34, -127.23) * mm, "construction": true});
            skLineSegment(sketch, "E104.1.0.13", {"start": v(-0.84, -129.23) * mm, "end": v(-4.34, -129.23) * mm, "construction": true});
            skLineSegment(sketch, "E104.1.0.14", {"start": v(1.16, -127.23) * mm, "end": v(1.16, -119.23) * mm, "construction": true});
            skLineSegment(sketch, "E104.1.0.15", {"start": v(13.66, -119.23) * mm, "end": v(-4.34, -119.23) * mm, "construction": true});
            skLineSegment(sketch, "E104.1.0.16", {"start": v(-0.84, -137.23) * mm, "end": v(-0.84, -129.23) * mm, "construction": true});
            skLineSegment(sketch, "E104.1.0.17", {"start": v(13.66, -137.23) * mm, "end": v(-4.34, -137.23) * mm, "construction": true});
            skLineSegment(sketch, "E104.1.0.18", {"start": v(1.16, -137.23) * mm, "end": v(1.16, -129.23) * mm, "construction": true});
            skLineSegment(sketch, "E104.1.0.19", {"start": v(8.16, -137.23) * mm, "end": v(8.16, -129.23) * mm, "construction": true});
            skLineSegment(sketch, "E104.1.0.20", {"start": v(-4.34, -137.23) * mm, "end": v(-4.34, -119.23) * mm, "construction": true});
            skLineSegment(sketch, "E104.1.0.21", {"start": v(8.16, -129.23) * mm, "end": v(1.16, -129.23) * mm, "construction": true});
            skLineSegment(sketch, "E104.1.0.22", {"start": v(10.16, -137.23) * mm, "end": v(8.16, -137.23) * mm, "construction": true});
            skLineSegment(sketch, "E104.1.0.23", {"start": v(13.66, -129.23) * mm, "end": v(13.66, -127.23) * mm, "construction": true});
            skLineSegment(sketch, "E104.1.0.24", {"start": v(1.16, -137.23) * mm, "end": v(-0.84, -137.23) * mm, "construction": true});
            skLineSegment(sketch, "E104.1.0.25", {"start": v(-4.34, -129.23) * mm, "end": v(-4.34, -127.23) * mm, "construction": true});
            skLineSegment(sketch, "E104.1.0.27", {"start": v(1.16, -119.23) * mm, "end": v(-0.84, -119.23) * mm, "construction": true});
            skLineSegment(sketch, "E104.2.0.0", {"start": v(25.16, -127.23) * mm, "end": v(25.16, -119.23) * mm, "construction": true});
            skLineSegment(sketch, "E104.2.0.2", {"start": v(39.66, -137.23) * mm, "end": v(39.66, -119.23) * mm, "construction": true});
            skLineSegment(sketch, "E104.2.0.3", {"start": v(36.16, -137.23) * mm, "end": v(36.16, -129.23) * mm, "construction": true});
            skPoint(sketch, "E104.2.0.4", {"position": v(26.16, -128.23) * mm});
            skLineSegment(sketch, "E104.2.0.5", {"start": v(34.16, -127.23) * mm, "end": v(34.16, -119.23) * mm, "construction": true});
            skLineSegment(sketch, "E104.2.0.6", {"start": v(36.16, -127.23) * mm, "end": v(36.16, -119.23) * mm, "construction": true});
            skLineSegment(sketch, "E104.2.0.7", {"start": v(34.16, -127.23) * mm, "end": v(27.16, -127.23) * mm, "construction": true});
            skLineSegment(sketch, "E104.2.0.8", {"start": v(39.66, -127.23) * mm, "end": v(36.16, -127.23) * mm, "construction": true});
            skLineSegment(sketch, "E104.2.0.9", {"start": v(39.66, -129.23) * mm, "end": v(36.16, -129.23) * mm, "construction": true});
            skLineSegment(sketch, "E104.2.0.10", {"start": v(36.16, -119.23) * mm, "end": v(34.16, -119.23) * mm, "construction": true});
            skPoint(sketch, "E104.2.0.11", {"position": v(35.16, -128.23) * mm});
            skLineSegment(sketch, "E104.2.0.12", {"start": v(25.16, -127.23) * mm, "end": v(21.66, -127.23) * mm, "construction": true});
            skLineSegment(sketch, "E104.2.0.13", {"start": v(25.16, -129.23) * mm, "end": v(21.66, -129.23) * mm, "construction": true});
            skLineSegment(sketch, "E104.2.0.14", {"start": v(27.16, -127.23) * mm, "end": v(27.16, -119.23) * mm, "construction": true});
            skLineSegment(sketch, "E104.2.0.15", {"start": v(39.66, -119.23) * mm, "end": v(21.66, -119.23) * mm, "construction": true});
            skLineSegment(sketch, "E104.2.0.16", {"start": v(25.16, -137.23) * mm, "end": v(25.16, -129.23) * mm, "construction": true});
            skLineSegment(sketch, "E104.2.0.17", {"start": v(39.66, -137.23) * mm, "end": v(21.66, -137.23) * mm, "construction": true});
            skLineSegment(sketch, "E104.2.0.18", {"start": v(27.16, -137.23) * mm, "end": v(27.16, -129.23) * mm, "construction": true});
            skLineSegment(sketch, "E104.2.0.19", {"start": v(34.16, -137.23) * mm, "end": v(34.16, -129.23) * mm, "construction": true});
            skLineSegment(sketch, "E104.2.0.20", {"start": v(21.66, -137.23) * mm, "end": v(21.66, -119.23) * mm, "construction": true});
            skLineSegment(sketch, "E104.2.0.21", {"start": v(34.16, -129.23) * mm, "end": v(27.16, -129.23) * mm, "construction": true});
            skLineSegment(sketch, "E104.2.0.22", {"start": v(36.16, -137.23) * mm, "end": v(34.16, -137.23) * mm, "construction": true});
            skLineSegment(sketch, "E104.2.0.23", {"start": v(39.66, -129.23) * mm, "end": v(39.66, -127.23) * mm, "construction": true});
            skLineSegment(sketch, "E104.2.0.24", {"start": v(27.16, -137.23) * mm, "end": v(25.16, -137.23) * mm, "construction": true});
            skLineSegment(sketch, "E104.2.0.25", {"start": v(21.66, -129.23) * mm, "end": v(21.66, -127.23) * mm, "construction": true});
            skLineSegment(sketch, "E104.2.0.27", {"start": v(27.16, -119.23) * mm, "end": v(25.16, -119.23) * mm, "construction": true});
            skLineSegment(sketch, "E104.direction1", {"start": v(-30.34, -137.23) * mm, "end": v(-4.34, -137.23) * mm, "construction": true});
            skLineSegment(sketch, "E105.1.0.0", {"start": v(13.66, -150.23) * mm, "end": v(10.18, -150.23) * mm, "construction": true});
            skLineSegment(sketch, "E105.1.0.1", {"start": v(1.18, -150.23) * mm, "end": v(1.18, -142.23) * mm, "construction": true});
            skLineSegment(sketch, "E105.1.0.2", {"start": v(8.18, -160.23) * mm, "end": v(8.18, -152.23) * mm, "construction": true});
            skLineSegment(sketch, "E105.1.0.3", {"start": v(-4.34, -160.23) * mm, "end": v(-4.34, -142.23) * mm, "construction": true});
            skLineSegment(sketch, "E105.1.0.4", {"start": v(-0.82, -160.23) * mm, "end": v(-0.82, -152.23) * mm, "construction": true});
            skLineSegment(sketch, "E105.1.0.5", {"start": v(13.66, -160.23) * mm, "end": v(13.66, -142.23) * mm, "construction": true});
            skLineSegment(sketch, "E105.1.0.6", {"start": v(8.18, -152.23) * mm, "end": v(1.18, -152.23) * mm, "construction": true});
            skLineSegment(sketch, "E105.1.0.7", {"start": v(1.18, -160.23) * mm, "end": v(1.18, -152.23) * mm, "construction": true});
            skLineSegment(sketch, "E105.1.0.9", {"start": v(10.18, -150.23) * mm, "end": v(10.18, -142.23) * mm, "construction": true});
            skLineSegment(sketch, "E105.1.0.10", {"start": v(13.66, -152.23) * mm, "end": v(10.18, -152.23) * mm, "construction": true});
            skPoint(sketch, "E105.1.0.11", {"position": v(9.18, -151.23) * mm});
            skLineSegment(sketch, "E105.1.0.12", {"start": v(-0.82, -152.23) * mm, "end": v(-4.34, -152.23) * mm, "construction": true});
            skLineSegment(sketch, "E105.1.0.14", {"start": v(8.18, -150.23) * mm, "end": v(1.18, -150.23) * mm, "construction": true});
            skPoint(sketch, "E105.1.0.15", {"position": v(0.18, -151.23) * mm});
            skLineSegment(sketch, "E105.1.0.16", {"start": v(10.18, -160.23) * mm, "end": v(10.18, -152.23) * mm, "construction": true});
            skLineSegment(sketch, "E105.1.0.17", {"start": v(13.66, -160.23) * mm, "end": v(-4.34, -160.23) * mm, "construction": true});
            skLineSegment(sketch, "E105.1.0.18", {"start": v(-0.82, -150.23) * mm, "end": v(-0.82, -142.23) * mm, "construction": true});
            skLineSegment(sketch, "E105.1.0.19", {"start": v(8.18, -150.23) * mm, "end": v(8.18, -142.23) * mm, "construction": true});
            skLineSegment(sketch, "E105.1.0.20", {"start": v(-0.82, -150.23) * mm, "end": v(-4.34, -150.23) * mm, "construction": true});
            skLineSegment(sketch, "E105.1.0.21", {"start": v(13.66, -142.23) * mm, "end": v(-4.34, -142.23) * mm, "construction": true});
            skLineSegment(sketch, "E105.1.0.22", {"start": v(1.18, -142.23) * mm, "end": v(-0.82, -142.23) * mm, "construction": true});
            skLineSegment(sketch, "E105.1.0.23", {"start": v(13.66, -152.23) * mm, "end": v(13.66, -150.23) * mm, "construction": true});
            skLineSegment(sketch, "E105.1.0.24", {"start": v(-4.34, -152.23) * mm, "end": v(-4.34, -150.23) * mm, "construction": true});
            skLineSegment(sketch, "E105.1.0.26", {"start": v(-4.34, -160.23) * mm, "end": v(-4.34, -142.23) * mm, "construction": true});
            skLineSegment(sketch, "E105.1.0.27", {"start": v(10.18, -142.23) * mm, "end": v(8.18, -142.23) * mm, "construction": true});
            skLineSegment(sketch, "E105.1.0.28", {"start": v(13.66, -160.23) * mm, "end": v(-4.34, -160.23) * mm, "construction": true});
            skLineSegment(sketch, "E105.1.0.29", {"start": v(13.66, -142.23) * mm, "end": v(-4.34, -142.23) * mm, "construction": true});
            skLineSegment(sketch, "E105.1.0.30", {"start": v(13.66, -160.23) * mm, "end": v(13.66, -142.23) * mm, "construction": true});
            skLineSegment(sketch, "E105.1.0.31", {"start": v(1.18, -160.23) * mm, "end": v(-0.82, -160.23) * mm, "construction": true});
            skLineSegment(sketch, "E105.1.0.32", {"start": v(10.18, -160.23) * mm, "end": v(8.18, -160.23) * mm, "construction": true});
            skLineSegment(sketch, "E105.2.0.0", {"start": v(39.66, -150.23) * mm, "end": v(36.18, -150.23) * mm, "construction": true});
            skLineSegment(sketch, "E105.2.0.1", {"start": v(27.18, -150.23) * mm, "end": v(27.18, -142.23) * mm, "construction": true});
            skLineSegment(sketch, "E105.2.0.2", {"start": v(34.18, -160.23) * mm, "end": v(34.18, -152.23) * mm, "construction": true});
            skLineSegment(sketch, "E105.2.0.3", {"start": v(21.66, -160.23) * mm, "end": v(21.66, -142.23) * mm, "construction": true});
            skLineSegment(sketch, "E105.2.0.4", {"start": v(25.18, -160.23) * mm, "end": v(25.18, -152.23) * mm, "construction": true});
            skLineSegment(sketch, "E105.2.0.5", {"start": v(39.66, -160.23) * mm, "end": v(39.66, -142.23) * mm, "construction": true});
            skLineSegment(sketch, "E105.2.0.6", {"start": v(34.18, -152.23) * mm, "end": v(27.18, -152.23) * mm, "construction": true});
            skLineSegment(sketch, "E105.2.0.7", {"start": v(27.18, -160.23) * mm, "end": v(27.18, -152.23) * mm, "construction": true});
            skLineSegment(sketch, "E105.2.0.9", {"start": v(36.18, -150.23) * mm, "end": v(36.18, -142.23) * mm, "construction": true});
            skLineSegment(sketch, "E105.2.0.10", {"start": v(39.66, -152.23) * mm, "end": v(36.18, -152.23) * mm, "construction": true});
            skPoint(sketch, "E105.2.0.11", {"position": v(35.18, -151.23) * mm});
            skLineSegment(sketch, "E105.2.0.12", {"start": v(25.18, -152.23) * mm, "end": v(21.66, -152.23) * mm, "construction": true});
            skLineSegment(sketch, "E105.2.0.14", {"start": v(34.18, -150.23) * mm, "end": v(27.18, -150.23) * mm, "construction": true});
            skPoint(sketch, "E105.2.0.15", {"position": v(26.18, -151.23) * mm});
            skLineSegment(sketch, "E105.2.0.16", {"start": v(36.18, -160.23) * mm, "end": v(36.18, -152.23) * mm, "construction": true});
            skLineSegment(sketch, "E105.2.0.17", {"start": v(39.66, -160.23) * mm, "end": v(21.66, -160.23) * mm, "construction": true});
            skLineSegment(sketch, "E105.2.0.18", {"start": v(25.18, -150.23) * mm, "end": v(25.18, -142.23) * mm, "construction": true});
            skLineSegment(sketch, "E105.2.0.19", {"start": v(34.18, -150.23) * mm, "end": v(34.18, -142.23) * mm, "construction": true});
            skLineSegment(sketch, "E105.2.0.20", {"start": v(25.18, -150.23) * mm, "end": v(21.66, -150.23) * mm, "construction": true});
            skLineSegment(sketch, "E105.2.0.21", {"start": v(39.66, -142.23) * mm, "end": v(21.66, -142.23) * mm, "construction": true});
            skLineSegment(sketch, "E105.2.0.22", {"start": v(27.18, -142.23) * mm, "end": v(25.18, -142.23) * mm, "construction": true});
            skLineSegment(sketch, "E105.2.0.23", {"start": v(39.66, -152.23) * mm, "end": v(39.66, -150.23) * mm, "construction": true});
            skLineSegment(sketch, "E105.2.0.24", {"start": v(21.66, -152.23) * mm, "end": v(21.66, -150.23) * mm, "construction": true});
            skLineSegment(sketch, "E105.2.0.26", {"start": v(21.66, -160.23) * mm, "end": v(21.66, -142.23) * mm, "construction": true});
            skLineSegment(sketch, "E105.2.0.27", {"start": v(36.18, -142.23) * mm, "end": v(34.18, -142.23) * mm, "construction": true});
            skLineSegment(sketch, "E105.2.0.28", {"start": v(39.66, -160.23) * mm, "end": v(21.66, -160.23) * mm, "construction": true});
            skLineSegment(sketch, "E105.2.0.29", {"start": v(39.66, -142.23) * mm, "end": v(21.66, -142.23) * mm, "construction": true});
            skLineSegment(sketch, "E105.2.0.30", {"start": v(39.66, -160.23) * mm, "end": v(39.66, -142.23) * mm, "construction": true});
            skLineSegment(sketch, "E105.2.0.31", {"start": v(27.18, -160.23) * mm, "end": v(25.18, -160.23) * mm, "construction": true});
            skLineSegment(sketch, "E105.2.0.32", {"start": v(36.18, -160.23) * mm, "end": v(34.18, -160.23) * mm, "construction": true});
            skLineSegment(sketch, "E105.direction1", {"start": v(-30.34, -160.23) * mm, "end": v(-4.34, -160.23) * mm, "construction": true});
            skLineSegment(sketch, "E106.bottom", {"start": v(-44.84, -133.23) * mm, "end": v(-46.84, -133.23) * mm});
            skLineSegment(sketch, "E106.top", {"start": v(-44.84, -123.23) * mm, "end": v(-46.84, -123.23) * mm});
            skLineSegment(sketch, "E106.left", {"start": v(-44.84, -133.23) * mm, "end": v(-44.84, -123.23) * mm});
            skLineSegment(sketch, "E106.right", {"start": v(-46.84, -133.23) * mm, "end": v(-46.84, -123.23) * mm});
            skLineSegment(sketch, "E107.bottom", {"start": v(-44.84, -156.23) * mm, "end": v(-46.84, -156.23) * mm});
            skLineSegment(sketch, "E107.top", {"start": v(-44.84, -146.23) * mm, "end": v(-46.84, -146.23) * mm});
            skLineSegment(sketch, "E107.left", {"start": v(-44.84, -156.23) * mm, "end": v(-44.84, -146.23) * mm});
            skLineSegment(sketch, "E107.right", {"start": v(-46.84, -156.23) * mm, "end": v(-46.84, -146.23) * mm});
            skCircle(sketch, "E108", {"center": v(-60.34, -124.73) * mm, "radius": 1.5 * mm});
            skPoint(sketch, "E108.centerSnap0", {"position": v(-61.34, -112.23) * mm});
            skCircle(sketch, "E109", {"center": v(-45.84, -128.23) * mm, "radius": 5 * mm});
            skCircle(sketch, "E110", {"center": v(-45.84, -151.23) * mm, "radius": 5 * mm});
            skCircle(sketch, "E111", {"center": v(-45.84, -174.23) * mm, "radius": 6.25 * mm});
            skCircle(sketch, "E112", {"center": v(-16.84, -174.23) * mm, "radius": 6.25 * mm});
            skCircle(sketch, "E113", {"center": v(-1.84, -174.23) * mm, "radius": 6.25 * mm});
            skCircle(sketch, "E114", {"center": v(25.16, -174.23) * mm, "radius": 6.25 * mm});
            skCircle(sketch, "E115", {"center": v(66.16, -174.23) * mm, "radius": 6.25 * mm});
            skCircle(sketch, "E116", {"center": v(51.16, -151.23) * mm, "radius": 6.25 * mm});
            skCircle(sketch, "E117", {"center": v(66.16, -128.23) * mm, "radius": 6.25 * mm});
            skCircle(sketch, "E118", {"center": v(-60.34, -174.73) * mm, "radius": 1.5 * mm});
            skCircle(sketch, "E119", {"center": v(79.66, -124.73) * mm, "radius": 1.5 * mm});
            skCircle(sketch, "E120", {"center": v(79.66, -174.73) * mm, "radius": 1.5 * mm});
            skSolve(sketch);
        }
        {
            var Q0;
            Q0=makeQuery(id+"F0.imprint","IMPRINT",FACE,{"disambiguationData":[TD([[makeQuery(id+"F0.imprint","IMPRINT",EDGE,{"derivedFrom":sQuery(id+"F0.wireOp",EDGE,"E0.bottom")}),-1.0]])]});
            var Q1;
            Q1=makeQuery(id+"F0.imprint","IMPRINT",FACE,{"disambiguationData":[TD([[makeQuery(id+"F0.imprint","IMPRINT",EDGE,{"derivedFrom":sQuery(id+"F0.wireOp",EDGE,"E23.bottom")}),-1.0]])]});
            var Q2;
            Q2=makeQuery(id+"F0.imprint","IMPRINT",FACE,{"disambiguationData":[TD([[makeQuery(id+"F0.imprint","IMPRINT",EDGE,{"derivedFrom":sQuery(id+"F0.wireOp",EDGE,"E35.bottom")}),-1.0]])]});
            var Q3;
            Q3=makeQuery(id+"F0.imprint","IMPRINT",FACE,{"disambiguationData":[TD([[makeQuery(id+"F0.imprint","IMPRINT",EDGE,{"derivedFrom":sQuery(id+"F0.wireOp",EDGE,"E48.1.0.0")}),-1.0]])]});
            var Q4;
            Q4=makeQuery(id+"F0.imprint","IMPRINT",FACE,{"disambiguationData":[TD([[makeQuery(id+"F0.imprint","IMPRINT",EDGE,{"derivedFrom":sQuery(id+"F0.wireOp",EDGE,"E48.2.0.0")}),-1.0]])]});
            var Q5;
            {var subQ3=sQuery(id+"F0.wireOp",EDGE,"E49.2.0.0");Q5=makeQuery(id+"F0.imprint","IMPRINT",FACE,{"disambiguationData":[TD([[makeQuery(id+"F0.imprint","IMPRINT",EDGE,{"derivedFrom":subQ3}),1.0]])]});}
            var Q6;
            {var subQ3=sQuery(id+"F0.wireOp",EDGE,"E49.1.0.0");Q6=makeQuery(id+"F0.imprint","IMPRINT",FACE,{"disambiguationData":[TD([[makeQuery(id+"F0.imprint","IMPRINT",EDGE,{"derivedFrom":subQ3}),1.0]])]});}
            var Q7;
            Q7=makeQuery(id+"F0.imprint","IMPRINT",FACE,{"disambiguationData":[TD([[makeQuery(id+"F0.imprint","IMPRINT",EDGE,{"derivedFrom":sQuery(id+"F0.wireOp",EDGE,"E50.bottom")}),-1.0]])]});
            var Q8;
            Q8=makeQuery(id+"F0.imprint","IMPRINT",FACE,{"disambiguationData":[TD([[makeQuery(id+"F0.imprint","IMPRINT",EDGE,{"derivedFrom":sQuery(id+"F0.wireOp",EDGE,"E51.bottom")}),-1.0]])]});
            extrude(context, id + "F2", {"entities" : qUnion([Q0, Q1, Q2, Q3, Q4, Q5, Q6, Q7, Q8]), "depth" : 1 * mm});
        }
        {
            var Q0;
            Q0=makeQuery(id+"F2.opExtrude","CAP_FACE",FACE,{"disambiguationData":[OSD([sQuery(id+"F0.wireOp",EDGE,"E0.bottom"),sQuery(id+"F0.wireOp",EDGE,"E0.top"),sQuery(id+"F0.wireOp",EDGE,"E0.left"),sQuery(id+"F0.wireOp",EDGE,"E0.right"),sQuery(id+"F0.wireOp",EDGE,"E5"),sQuery(id+"F0.wireOp",EDGE,"E6"),sQuery(id+"F0.wireOp",EDGE,"E7"),sQuery(id+"F0.wireOp",EDGE,"E10"),sQuery(id+"F0.wireOp",EDGE,"E11"),sQuery(id+"F0.wireOp",EDGE,"E12"),sQuery(id+"F0.wireOp",EDGE,"E13"),sQuery(id+"F0.wireOp",EDGE,"E14"),sQuery(id+"F0.wireOp",EDGE,"E15"),sQuery(id+"F0.wireOp",EDGE,"E16"),sQuery(id+"F0.wireOp",EDGE,"E17.bottom"),sQuery(id+"F0.wireOp",EDGE,"E17.top"),sQuery(id+"F0.wireOp",EDGE,"E17.left"),sQuery(id+"F0.wireOp",EDGE,"E17.right"),sQuery(id+"F0.wireOp",EDGE,"E18"),sQuery(id+"F0.wireOp",EDGE,"E19"),sQuery(id+"F0.wireOp",EDGE,"E21.bottom"),sQuery(id+"F0.wireOp",EDGE,"E21.top"),sQuery(id+"F0.wireOp",EDGE,"E21.left"),sQuery(id+"F0.wireOp",EDGE,"E21.right"),sQuery(id+"F0.wireOp",EDGE,"E23.bottom"),sQuery(id+"F0.wireOp",EDGE,"E23.top"),sQuery(id+"F0.wireOp",EDGE,"E24.left"),sQuery(id+"F0.wireOp",EDGE,"E24.right"),sQuery(id+"F0.wireOp",EDGE,"E25.left"),sQuery(id+"F0.wireOp",EDGE,"E25.right"),sQuery(id+"F0.wireOp",EDGE,"E26.trimOffspring"),sQuery(id+"F0.wireOp",EDGE,"E27.trimOffspring"),sQuery(id+"F0.wireOp",EDGE,"E28.trimOffspring"),sQuery(id+"F0.wireOp",EDGE,"E29.trimOffspring"),sQuery(id+"F0.wireOp",EDGE,"E30.trimOffspring"),sQuery(id+"F0.wireOp",EDGE,"E31.trimOffspring"),sQuery(id+"F0.wireOp",EDGE,"E32.trimOffspring"),sQuery(id+"F0.wireOp",EDGE,"E33.trimOffspring"),sQuery(id+"F0.wireOp",EDGE,"E22.bottom"),sQuery(id+"F0.wireOp",EDGE,"E22.top"),sQuery(id+"F0.wireOp",EDGE,"E22.left"),sQuery(id+"F0.wireOp",EDGE,"E22.right"),sQuery(id+"F0.wireOp",EDGE,"E35.bottom"),sQuery(id+"F0.wireOp",EDGE,"E35.top"),sQuery(id+"F0.wireOp",EDGE,"E36.left"),sQuery(id+"F0.wireOp",EDGE,"E36.right"),sQuery(id+"F0.wireOp",EDGE,"E37.left"),sQuery(id+"F0.wireOp",EDGE,"E37.right"),sQuery(id+"F0.wireOp",EDGE,"E38.trimOffspring"),sQuery(id+"F0.wireOp",EDGE,"E39.trimOffspring"),sQuery(id+"F0.wireOp",EDGE,"E40.trimOffspring"),sQuery(id+"F0.wireOp",EDGE,"E41.trimOffspring"),sQuery(id+"F0.wireOp",EDGE,"E42.trimOffspring"),sQuery(id+"F0.wireOp",EDGE,"E43.trimOffspring"),sQuery(id+"F0.wireOp",EDGE,"E44.trimOffspring"),sQuery(id+"F0.wireOp",EDGE,"E45.trimOffspring"),sQuery(id+"F0.wireOp",EDGE,"E46.bottom"),sQuery(id+"F0.wireOp",EDGE,"E46.top"),sQuery(id+"F0.wireOp",EDGE,"E46.left"),sQuery(id+"F0.wireOp",EDGE,"E46.right"),sQuery(id+"F0.wireOp",EDGE,"E47.bottom"),sQuery(id+"F0.wireOp",EDGE,"E47.top"),sQuery(id+"F0.wireOp",EDGE,"E47.left"),sQuery(id+"F0.wireOp",EDGE,"E47.right"),sQuery(id+"F0.wireOp",EDGE,"E48.1.0.0"),sQuery(id+"F0.wireOp",EDGE,"E48.1.0.2"),sQuery(id+"F0.wireOp",EDGE,"E48.1.0.3"),sQuery(id+"F0.wireOp",EDGE,"E48.1.0.5"),sQuery(id+"F0.wireOp",EDGE,"E48.1.0.6"),sQuery(id+"F0.wireOp",EDGE,"E48.1.0.7"),sQuery(id+"F0.wireOp",EDGE,"E48.1.0.8"),sQuery(id+"F0.wireOp",EDGE,"E48.1.0.9"),sQuery(id+"F0.wireOp",EDGE,"E48.1.0.12"),sQuery(id+"F0.wireOp",EDGE,"E48.1.0.13"),sQuery(id+"F0.wireOp",EDGE,"E48.1.0.14"),sQuery(id+"F0.wireOp",EDGE,"E48.1.0.15"),sQuery(id+"F0.wireOp",EDGE,"E48.1.0.16"),sQuery(id+"F0.wireOp",EDGE,"E48.1.0.17"),sQuery(id+"F0.wireOp",EDGE,"E48.1.0.18"),sQuery(id+"F0.wireOp",EDGE,"E48.1.0.19"),sQuery(id+"F0.wireOp",EDGE,"E48.1.0.20"),sQuery(id+"F0.wireOp",EDGE,"E48.1.0.21"),sQuery(id+"F0.wireOp",EDGE,"E48.2.0.0"),sQuery(id+"F0.wireOp",EDGE,"E48.2.0.2"),sQuery(id+"F0.wireOp",EDGE,"E48.2.0.3"),sQuery(id+"F0.wireOp",EDGE,"E48.2.0.5"),sQuery(id+"F0.wireOp",EDGE,"E48.2.0.6"),sQuery(id+"F0.wireOp",EDGE,"E48.2.0.7"),sQuery(id+"F0.wireOp",EDGE,"E48.2.0.8"),sQuery(id+"F0.wireOp",EDGE,"E48.2.0.9"),sQuery(id+"F0.wireOp",EDGE,"E48.2.0.12"),sQuery(id+"F0.wireOp",EDGE,"E48.2.0.13"),sQuery(id+"F0.wireOp",EDGE,"E48.2.0.14"),sQuery(id+"F0.wireOp",EDGE,"E48.2.0.15"),sQuery(id+"F0.wireOp",EDGE,"E48.2.0.16"),sQuery(id+"F0.wireOp",EDGE,"E48.2.0.17"),sQuery(id+"F0.wireOp",EDGE,"E48.2.0.18"),sQuery(id+"F0.wireOp",EDGE,"E48.2.0.19"),sQuery(id+"F0.wireOp",EDGE,"E48.2.0.20"),sQuery(id+"F0.wireOp",EDGE,"E48.2.0.21"),sQuery(id+"F0.wireOp",EDGE,"E49.1.0.0"),sQuery(id+"F0.wireOp",EDGE,"E49.1.0.1"),sQuery(id+"F0.wireOp",EDGE,"E49.1.0.2"),sQuery(id+"F0.wireOp",EDGE,"E49.1.0.4"),sQuery(id+"F0.wireOp",EDGE,"E49.1.0.6"),sQuery(id+"F0.wireOp",EDGE,"E49.1.0.7"),sQuery(id+"F0.wireOp",EDGE,"E49.1.0.9"),sQuery(id+"F0.wireOp",EDGE,"E49.1.0.10"),sQuery(id+"F0.wireOp",EDGE,"E49.1.0.12"),sQuery(id+"F0.wireOp",EDGE,"E49.1.0.14"),sQuery(id+"F0.wireOp",EDGE,"E49.1.0.16"),sQuery(id+"F0.wireOp",EDGE,"E49.1.0.18"),sQuery(id+"F0.wireOp",EDGE,"E49.1.0.19"),sQuery(id+"F0.wireOp",EDGE,"E49.1.0.20"),sQuery(id+"F0.wireOp",EDGE,"E49.1.0.26"),sQuery(id+"F0.wireOp",EDGE,"E49.1.0.28"),sQuery(id+"F0.wireOp",EDGE,"E49.1.0.29"),sQuery(id+"F0.wireOp",EDGE,"E49.1.0.30"),sQuery(id+"F0.wireOp",EDGE,"E49.2.0.0"),sQuery(id+"F0.wireOp",EDGE,"E49.2.0.1"),sQuery(id+"F0.wireOp",EDGE,"E49.2.0.2"),sQuery(id+"F0.wireOp",EDGE,"E49.2.0.4"),sQuery(id+"F0.wireOp",EDGE,"E49.2.0.6"),sQuery(id+"F0.wireOp",EDGE,"E49.2.0.7"),sQuery(id+"F0.wireOp",EDGE,"E49.2.0.9"),sQuery(id+"F0.wireOp",EDGE,"E49.2.0.10"),sQuery(id+"F0.wireOp",EDGE,"E49.2.0.12"),sQuery(id+"F0.wireOp",EDGE,"E49.2.0.14"),sQuery(id+"F0.wireOp",EDGE,"E49.2.0.16"),sQuery(id+"F0.wireOp",EDGE,"E49.2.0.18"),sQuery(id+"F0.wireOp",EDGE,"E49.2.0.19"),sQuery(id+"F0.wireOp",EDGE,"E49.2.0.20"),sQuery(id+"F0.wireOp",EDGE,"E49.2.0.26"),sQuery(id+"F0.wireOp",EDGE,"E49.2.0.28"),sQuery(id+"F0.wireOp",EDGE,"E49.2.0.29"),sQuery(id+"F0.wireOp",EDGE,"E49.2.0.30")])],"isStart":false});
            extrude(context, id + "F3", {"entities" : qUnion([Q0]), "operationType" : NewBodyOperationType.ADD, "depth" : 5 * mm});
        }
        {
            var Q0;
            Q0=makeQuery(id+"F3.opExtrude","CAP_FACE",FACE,{"disambiguationData":[OSD([sQuery(id+"F0.wireOp",EDGE,"E0.bottom"),sQuery(id+"F0.wireOp",EDGE,"E0.top"),sQuery(id+"F0.wireOp",EDGE,"E0.left"),sQuery(id+"F0.wireOp",EDGE,"E0.right"),sQuery(id+"F0.wireOp",EDGE,"E5"),sQuery(id+"F0.wireOp",EDGE,"E6"),sQuery(id+"F0.wireOp",EDGE,"E7"),sQuery(id+"F0.wireOp",EDGE,"E10"),sQuery(id+"F0.wireOp",EDGE,"E11"),sQuery(id+"F0.wireOp",EDGE,"E12"),sQuery(id+"F0.wireOp",EDGE,"E13"),sQuery(id+"F0.wireOp",EDGE,"E14"),sQuery(id+"F0.wireOp",EDGE,"E15"),sQuery(id+"F0.wireOp",EDGE,"E16"),sQuery(id+"F0.wireOp",EDGE,"E17.bottom"),sQuery(id+"F0.wireOp",EDGE,"E17.top"),sQuery(id+"F0.wireOp",EDGE,"E17.left"),sQuery(id+"F0.wireOp",EDGE,"E17.right"),sQuery(id+"F0.wireOp",EDGE,"E18"),sQuery(id+"F0.wireOp",EDGE,"E19"),sQuery(id+"F0.wireOp",EDGE,"E21.bottom"),sQuery(id+"F0.wireOp",EDGE,"E21.top"),sQuery(id+"F0.wireOp",EDGE,"E21.left"),sQuery(id+"F0.wireOp",EDGE,"E21.right"),sQuery(id+"F0.wireOp",EDGE,"E23.bottom"),sQuery(id+"F0.wireOp",EDGE,"E23.top"),sQuery(id+"F0.wireOp",EDGE,"E24.left"),sQuery(id+"F0.wireOp",EDGE,"E24.right"),sQuery(id+"F0.wireOp",EDGE,"E25.left"),sQuery(id+"F0.wireOp",EDGE,"E25.right"),sQuery(id+"F0.wireOp",EDGE,"E26.trimOffspring"),sQuery(id+"F0.wireOp",EDGE,"E27.trimOffspring"),sQuery(id+"F0.wireOp",EDGE,"E28.trimOffspring"),sQuery(id+"F0.wireOp",EDGE,"E29.trimOffspring"),sQuery(id+"F0.wireOp",EDGE,"E30.trimOffspring"),sQuery(id+"F0.wireOp",EDGE,"E31.trimOffspring"),sQuery(id+"F0.wireOp",EDGE,"E32.trimOffspring"),sQuery(id+"F0.wireOp",EDGE,"E33.trimOffspring"),sQuery(id+"F0.wireOp",EDGE,"E22.bottom"),sQuery(id+"F0.wireOp",EDGE,"E22.top"),sQuery(id+"F0.wireOp",EDGE,"E22.left"),sQuery(id+"F0.wireOp",EDGE,"E22.right"),sQuery(id+"F0.wireOp",EDGE,"E35.bottom"),sQuery(id+"F0.wireOp",EDGE,"E35.top"),sQuery(id+"F0.wireOp",EDGE,"E36.left"),sQuery(id+"F0.wireOp",EDGE,"E36.right"),sQuery(id+"F0.wireOp",EDGE,"E37.left"),sQuery(id+"F0.wireOp",EDGE,"E37.right"),sQuery(id+"F0.wireOp",EDGE,"E38.trimOffspring"),sQuery(id+"F0.wireOp",EDGE,"E39.trimOffspring"),sQuery(id+"F0.wireOp",EDGE,"E40.trimOffspring"),sQuery(id+"F0.wireOp",EDGE,"E41.trimOffspring"),sQuery(id+"F0.wireOp",EDGE,"E42.trimOffspring"),sQuery(id+"F0.wireOp",EDGE,"E43.trimOffspring"),sQuery(id+"F0.wireOp",EDGE,"E44.trimOffspring"),sQuery(id+"F0.wireOp",EDGE,"E45.trimOffspring"),sQuery(id+"F0.wireOp",EDGE,"E46.bottom"),sQuery(id+"F0.wireOp",EDGE,"E46.top"),sQuery(id+"F0.wireOp",EDGE,"E46.left"),sQuery(id+"F0.wireOp",EDGE,"E46.right"),sQuery(id+"F0.wireOp",EDGE,"E47.bottom"),sQuery(id+"F0.wireOp",EDGE,"E47.top"),sQuery(id+"F0.wireOp",EDGE,"E47.left"),sQuery(id+"F0.wireOp",EDGE,"E47.right"),sQuery(id+"F0.wireOp",EDGE,"E48.1.0.0"),sQuery(id+"F0.wireOp",EDGE,"E48.1.0.2"),sQuery(id+"F0.wireOp",EDGE,"E48.1.0.3"),sQuery(id+"F0.wireOp",EDGE,"E48.1.0.5"),sQuery(id+"F0.wireOp",EDGE,"E48.1.0.6"),sQuery(id+"F0.wireOp",EDGE,"E48.1.0.7"),sQuery(id+"F0.wireOp",EDGE,"E48.1.0.8"),sQuery(id+"F0.wireOp",EDGE,"E48.1.0.9"),sQuery(id+"F0.wireOp",EDGE,"E48.1.0.12"),sQuery(id+"F0.wireOp",EDGE,"E48.1.0.13"),sQuery(id+"F0.wireOp",EDGE,"E48.1.0.14"),sQuery(id+"F0.wireOp",EDGE,"E48.1.0.15"),sQuery(id+"F0.wireOp",EDGE,"E48.1.0.16"),sQuery(id+"F0.wireOp",EDGE,"E48.1.0.17"),sQuery(id+"F0.wireOp",EDGE,"E48.1.0.18"),sQuery(id+"F0.wireOp",EDGE,"E48.1.0.19"),sQuery(id+"F0.wireOp",EDGE,"E48.1.0.20"),sQuery(id+"F0.wireOp",EDGE,"E48.1.0.21"),sQuery(id+"F0.wireOp",EDGE,"E48.2.0.0"),sQuery(id+"F0.wireOp",EDGE,"E48.2.0.2"),sQuery(id+"F0.wireOp",EDGE,"E48.2.0.3"),sQuery(id+"F0.wireOp",EDGE,"E48.2.0.5"),sQuery(id+"F0.wireOp",EDGE,"E48.2.0.6"),sQuery(id+"F0.wireOp",EDGE,"E48.2.0.7"),sQuery(id+"F0.wireOp",EDGE,"E48.2.0.8"),sQuery(id+"F0.wireOp",EDGE,"E48.2.0.9"),sQuery(id+"F0.wireOp",EDGE,"E48.2.0.12"),sQuery(id+"F0.wireOp",EDGE,"E48.2.0.13"),sQuery(id+"F0.wireOp",EDGE,"E48.2.0.14"),sQuery(id+"F0.wireOp",EDGE,"E48.2.0.15"),sQuery(id+"F0.wireOp",EDGE,"E48.2.0.16"),sQuery(id+"F0.wireOp",EDGE,"E48.2.0.17"),sQuery(id+"F0.wireOp",EDGE,"E48.2.0.18"),sQuery(id+"F0.wireOp",EDGE,"E48.2.0.19"),sQuery(id+"F0.wireOp",EDGE,"E48.2.0.20"),sQuery(id+"F0.wireOp",EDGE,"E48.2.0.21"),sQuery(id+"F0.wireOp",EDGE,"E49.1.0.0"),sQuery(id+"F0.wireOp",EDGE,"E49.1.0.1"),sQuery(id+"F0.wireOp",EDGE,"E49.1.0.2"),sQuery(id+"F0.wireOp",EDGE,"E49.1.0.4"),sQuery(id+"F0.wireOp",EDGE,"E49.1.0.6"),sQuery(id+"F0.wireOp",EDGE,"E49.1.0.7"),sQuery(id+"F0.wireOp",EDGE,"E49.1.0.9"),sQuery(id+"F0.wireOp",EDGE,"E49.1.0.10"),sQuery(id+"F0.wireOp",EDGE,"E49.1.0.12"),sQuery(id+"F0.wireOp",EDGE,"E49.1.0.14"),sQuery(id+"F0.wireOp",EDGE,"E49.1.0.16"),sQuery(id+"F0.wireOp",EDGE,"E49.1.0.18"),sQuery(id+"F0.wireOp",EDGE,"E49.1.0.19"),sQuery(id+"F0.wireOp",EDGE,"E49.1.0.20"),sQuery(id+"F0.wireOp",EDGE,"E49.1.0.26"),sQuery(id+"F0.wireOp",EDGE,"E49.1.0.28"),sQuery(id+"F0.wireOp",EDGE,"E49.1.0.29"),sQuery(id+"F0.wireOp",EDGE,"E49.1.0.30"),sQuery(id+"F0.wireOp",EDGE,"E49.2.0.0"),sQuery(id+"F0.wireOp",EDGE,"E49.2.0.1"),sQuery(id+"F0.wireOp",EDGE,"E49.2.0.2"),sQuery(id+"F0.wireOp",EDGE,"E49.2.0.4"),sQuery(id+"F0.wireOp",EDGE,"E49.2.0.6"),sQuery(id+"F0.wireOp",EDGE,"E49.2.0.7"),sQuery(id+"F0.wireOp",EDGE,"E49.2.0.9"),sQuery(id+"F0.wireOp",EDGE,"E49.2.0.10"),sQuery(id+"F0.wireOp",EDGE,"E49.2.0.12"),sQuery(id+"F0.wireOp",EDGE,"E49.2.0.14"),sQuery(id+"F0.wireOp",EDGE,"E49.2.0.16"),sQuery(id+"F0.wireOp",EDGE,"E49.2.0.18"),sQuery(id+"F0.wireOp",EDGE,"E49.2.0.19"),sQuery(id+"F0.wireOp",EDGE,"E49.2.0.20"),sQuery(id+"F0.wireOp",EDGE,"E49.2.0.26"),sQuery(id+"F0.wireOp",EDGE,"E49.2.0.28"),sQuery(id+"F0.wireOp",EDGE,"E49.2.0.29"),sQuery(id+"F0.wireOp",EDGE,"E49.2.0.30")])],"isStart":false});
            var sketch = newSketch(context, id + "F4", { "sketchPlane" : qUnion([Q0])});
            skPoint(sketch, "E121.0", {"position": v(-111.5, 1.96) * mm});
            skLineSegment(sketch, "E122.bottom", {"start": v(-102.5, -7.04) * mm, "end": v(-120.5, -7.04) * mm});
            skLineSegment(sketch, "E122.top", {"start": v(-102.5, 10.96) * mm, "end": v(-120.5, 10.96) * mm});
            skLineSegment(sketch, "E122.left", {"start": v(-102.5, -7.04) * mm, "end": v(-102.5, 10.96) * mm});
            skLineSegment(sketch, "E122.right", {"start": v(-120.5, -7.04) * mm, "end": v(-120.5, 10.96) * mm});
            skPoint(sketch, "E123.0", {"position": v(-111.5, -21.04) * mm});
            skLineSegment(sketch, "E124.bottom", {"start": v(-102.5, -30.04) * mm, "end": v(-120.5, -30.04) * mm});
            skLineSegment(sketch, "E124.top", {"start": v(-102.5, -12.04) * mm, "end": v(-120.5, -12.04) * mm});
            skLineSegment(sketch, "E124.left", {"start": v(-102.5, -30.04) * mm, "end": v(-102.5, -12.04) * mm});
            skLineSegment(sketch, "E124.right", {"start": v(-120.5, -30.04) * mm, "end": v(-120.5, -12.04) * mm});
            skPoint(sketch, "E125.0", {"position": v(-121.5, -21.04) * mm});
            skPoint(sketch, "E125.1", {"position": v(-121.5, 1.96) * mm});
            skLineSegment(sketch, "E126.bottom", {"start": v(-120.5, -3.04) * mm, "end": v(-122.5, -3.04) * mm});
            skLineSegment(sketch, "E126.top", {"start": v(-120.5, 6.96) * mm, "end": v(-122.5, 6.96) * mm});
            skLineSegment(sketch, "E126.left", {"start": v(-120.5, -3.04) * mm, "end": v(-120.5, 6.96) * mm});
            skLineSegment(sketch, "E126.right", {"start": v(-122.5, -3.04) * mm, "end": v(-122.5, 6.96) * mm});
            skPoint(sketch, "E127.0", {"position": v(-101.5, 1.96) * mm});
            skLineSegment(sketch, "E128.bottom", {"start": v(-102.5, -3.04) * mm, "end": v(-100.5, -3.04) * mm});
            skLineSegment(sketch, "E128.top", {"start": v(-102.5, 6.96) * mm, "end": v(-100.5, 6.96) * mm});
            skLineSegment(sketch, "E128.left", {"start": v(-102.5, -3.04) * mm, "end": v(-102.5, 6.96) * mm});
            skLineSegment(sketch, "E128.right", {"start": v(-100.5, -3.04) * mm, "end": v(-100.5, 6.96) * mm});
            skPoint(sketch, "E129.1.0.0", {"position": v(-75.5, 1.96) * mm});
            skPoint(sketch, "E129.1.0.1", {"position": v(-95.5, 1.96) * mm});
            skLineSegment(sketch, "E129.1.0.2", {"start": v(-76.5, -3.04) * mm, "end": v(-74.5, -3.04) * mm});
            skLineSegment(sketch, "E129.1.0.3", {"start": v(-76.5, 6.96) * mm, "end": v(-74.5, 6.96) * mm});
            skLineSegment(sketch, "E129.1.0.4", {"start": v(-94.5, -3.04) * mm, "end": v(-96.5, -3.04) * mm});
            skLineSegment(sketch, "E129.1.0.5", {"start": v(-76.5, 10.96) * mm, "end": v(-94.5, 10.96) * mm});
            skLineSegment(sketch, "E129.1.0.6", {"start": v(-76.5, -7.04) * mm, "end": v(-76.5, 10.96) * mm});
            skPoint(sketch, "E129.1.0.7", {"position": v(-85.5, 1.96) * mm});
            skLineSegment(sketch, "E129.1.0.8", {"start": v(-94.5, 6.96) * mm, "end": v(-96.5, 6.96) * mm});
            skLineSegment(sketch, "E129.1.0.9", {"start": v(-76.5, -7.04) * mm, "end": v(-94.5, -7.04) * mm});
            skLineSegment(sketch, "E129.1.0.10", {"start": v(-94.5, -7.04) * mm, "end": v(-94.5, 10.96) * mm});
            skLineSegment(sketch, "E129.1.0.11", {"start": v(-96.5, -3.04) * mm, "end": v(-96.5, 6.96) * mm});
            skLineSegment(sketch, "E129.1.0.12", {"start": v(-74.5, -3.04) * mm, "end": v(-74.5, 6.96) * mm});
            skPoint(sketch, "E129.1.0.13", {"position": v(-95.5, 1.96) * mm});
            skLineSegment(sketch, "E129.1.0.14", {"start": v(-76.5, -3.04) * mm, "end": v(-76.5, 6.96) * mm});
            skPoint(sketch, "E129.1.0.15", {"position": v(-75.5, 1.96) * mm});
            skLineSegment(sketch, "E129.1.0.16", {"start": v(-94.5, -3.04) * mm, "end": v(-94.5, 6.96) * mm});
            skPoint(sketch, "E129.1.0.17", {"position": v(-85.5, 1.96) * mm});
            skPoint(sketch, "E129.2.0.0", {"position": v(-49.5, 1.96) * mm});
            skPoint(sketch, "E129.2.0.1", {"position": v(-69.5, 1.96) * mm});
            skLineSegment(sketch, "E129.2.0.2", {"start": v(-50.5, -3.04) * mm, "end": v(-48.5, -3.04) * mm});
            skLineSegment(sketch, "E129.2.0.3", {"start": v(-50.5, 6.96) * mm, "end": v(-48.5, 6.96) * mm});
            skLineSegment(sketch, "E129.2.0.4", {"start": v(-68.5, -3.04) * mm, "end": v(-70.5, -3.04) * mm});
            skLineSegment(sketch, "E129.2.0.5", {"start": v(-50.5, 10.96) * mm, "end": v(-68.5, 10.96) * mm});
            skLineSegment(sketch, "E129.2.0.6", {"start": v(-50.5, -7.04) * mm, "end": v(-50.5, 10.96) * mm});
            skPoint(sketch, "E129.2.0.7", {"position": v(-59.5, 1.96) * mm});
            skLineSegment(sketch, "E129.2.0.8", {"start": v(-68.5, 6.96) * mm, "end": v(-70.5, 6.96) * mm});
            skLineSegment(sketch, "E129.2.0.9", {"start": v(-50.5, -7.04) * mm, "end": v(-68.5, -7.04) * mm});
            skLineSegment(sketch, "E129.2.0.10", {"start": v(-68.5, -7.04) * mm, "end": v(-68.5, 10.96) * mm});
            skLineSegment(sketch, "E129.2.0.11", {"start": v(-70.5, -3.04) * mm, "end": v(-70.5, 6.96) * mm});
            skLineSegment(sketch, "E129.2.0.12", {"start": v(-48.5, -3.04) * mm, "end": v(-48.5, 6.96) * mm});
            skPoint(sketch, "E129.2.0.13", {"position": v(-69.5, 1.96) * mm});
            skLineSegment(sketch, "E129.2.0.14", {"start": v(-50.5, -3.04) * mm, "end": v(-50.5, 6.96) * mm});
            skPoint(sketch, "E129.2.0.15", {"position": v(-49.5, 1.96) * mm});
            skLineSegment(sketch, "E129.2.0.16", {"start": v(-68.5, -3.04) * mm, "end": v(-68.5, 6.96) * mm});
            skPoint(sketch, "E129.2.0.17", {"position": v(-59.5, 1.96) * mm});
            skLineSegment(sketch, "E129.direction1", {"start": v(-120.5, -7.04) * mm, "end": v(-94.5, -7.04) * mm, "construction": true});
            skLineSegment(sketch, "E130.bottom", {"start": v(-120.5, -26.04) * mm, "end": v(-122.5, -26.04) * mm});
            skLineSegment(sketch, "E130.top", {"start": v(-120.5, -16.04) * mm, "end": v(-122.5, -16.04) * mm});
            skLineSegment(sketch, "E130.left", {"start": v(-120.5, -26.04) * mm, "end": v(-120.5, -16.04) * mm});
            skLineSegment(sketch, "E130.right", {"start": v(-122.5, -26.04) * mm, "end": v(-122.5, -16.04) * mm});
            skPoint(sketch, "E131.0", {"position": v(-101.5, -21.04) * mm});
            skLineSegment(sketch, "E132.bottom", {"start": v(-102.5, -16.04) * mm, "end": v(-100.5, -16.04) * mm});
            skLineSegment(sketch, "E132.top", {"start": v(-102.5, -26.04) * mm, "end": v(-100.5, -26.04) * mm});
            skLineSegment(sketch, "E132.left", {"start": v(-102.5, -16.04) * mm, "end": v(-102.5, -26.04) * mm});
            skLineSegment(sketch, "E132.right", {"start": v(-100.5, -16.04) * mm, "end": v(-100.5, -26.04) * mm});
            skPoint(sketch, "E133.1.0.0", {"position": v(-95.5, -21.04) * mm});
            skLineSegment(sketch, "E133.1.0.1", {"start": v(-74.5, -16.04) * mm, "end": v(-74.5, -26.04) * mm});
            skLineSegment(sketch, "E133.1.0.2", {"start": v(-76.5, -26.04) * mm, "end": v(-74.5, -26.04) * mm});
            skLineSegment(sketch, "E133.1.0.3", {"start": v(-76.5, -30.04) * mm, "end": v(-76.5, -12.04) * mm});
            skLineSegment(sketch, "E133.1.0.4", {"start": v(-94.5, -30.04) * mm, "end": v(-94.5, -12.04) * mm});
            skLineSegment(sketch, "E133.1.0.5", {"start": v(-94.5, -16.04) * mm, "end": v(-96.5, -16.04) * mm});
            skLineSegment(sketch, "E133.1.0.6", {"start": v(-94.5, -26.04) * mm, "end": v(-96.5, -26.04) * mm});
            skLineSegment(sketch, "E133.1.0.7", {"start": v(-76.5, -30.04) * mm, "end": v(-94.5, -30.04) * mm});
            skPoint(sketch, "E133.1.0.8", {"position": v(-75.5, -21.04) * mm});
            skLineSegment(sketch, "E133.1.0.9", {"start": v(-76.5, -12.04) * mm, "end": v(-94.5, -12.04) * mm});
            skLineSegment(sketch, "E133.1.0.10", {"start": v(-76.5, -16.04) * mm, "end": v(-74.5, -16.04) * mm});
            skPoint(sketch, "E133.1.0.11", {"position": v(-85.5, -21.04) * mm});
            skLineSegment(sketch, "E133.1.0.12", {"start": v(-96.5, -26.04) * mm, "end": v(-96.5, -16.04) * mm});
            skLineSegment(sketch, "E133.1.0.13", {"start": v(-76.5, -16.04) * mm, "end": v(-76.5, -26.04) * mm});
            skLineSegment(sketch, "E133.1.0.14", {"start": v(-94.5, -26.04) * mm, "end": v(-94.5, -16.04) * mm});
            skPoint(sketch, "E133.1.0.15", {"position": v(-85.5, -21.04) * mm});
            skPoint(sketch, "E133.1.0.16", {"position": v(-75.5, -21.04) * mm});
            skPoint(sketch, "E133.1.0.17", {"position": v(-95.5, -21.04) * mm});
            skPoint(sketch, "E133.2.0.0", {"position": v(-69.5, -21.04) * mm});
            skLineSegment(sketch, "E133.2.0.1", {"start": v(-48.5, -16.04) * mm, "end": v(-48.5, -26.04) * mm});
            skLineSegment(sketch, "E133.2.0.2", {"start": v(-50.5, -26.04) * mm, "end": v(-48.5, -26.04) * mm});
            skLineSegment(sketch, "E133.2.0.3", {"start": v(-50.5, -30.04) * mm, "end": v(-50.5, -12.04) * mm});
            skLineSegment(sketch, "E133.2.0.4", {"start": v(-68.5, -30.04) * mm, "end": v(-68.5, -12.04) * mm});
            skLineSegment(sketch, "E133.2.0.5", {"start": v(-68.5, -16.04) * mm, "end": v(-70.5, -16.04) * mm});
            skLineSegment(sketch, "E133.2.0.6", {"start": v(-68.5, -26.04) * mm, "end": v(-70.5, -26.04) * mm});
            skLineSegment(sketch, "E133.2.0.7", {"start": v(-50.5, -30.04) * mm, "end": v(-68.5, -30.04) * mm});
            skPoint(sketch, "E133.2.0.8", {"position": v(-49.5, -21.04) * mm});
            skLineSegment(sketch, "E133.2.0.9", {"start": v(-50.5, -12.04) * mm, "end": v(-68.5, -12.04) * mm});
            skLineSegment(sketch, "E133.2.0.10", {"start": v(-50.5, -16.04) * mm, "end": v(-48.5, -16.04) * mm});
            skPoint(sketch, "E133.2.0.11", {"position": v(-59.5, -21.04) * mm});
            skLineSegment(sketch, "E133.2.0.12", {"start": v(-70.5, -26.04) * mm, "end": v(-70.5, -16.04) * mm});
            skLineSegment(sketch, "E133.2.0.13", {"start": v(-50.5, -16.04) * mm, "end": v(-50.5, -26.04) * mm});
            skLineSegment(sketch, "E133.2.0.14", {"start": v(-68.5, -26.04) * mm, "end": v(-68.5, -16.04) * mm});
            skPoint(sketch, "E133.2.0.15", {"position": v(-59.5, -21.04) * mm});
            skPoint(sketch, "E133.2.0.16", {"position": v(-49.5, -21.04) * mm});
            skPoint(sketch, "E133.2.0.17", {"position": v(-69.5, -21.04) * mm});
            skLineSegment(sketch, "E133.direction1", {"start": v(-120.5, -30.04) * mm, "end": v(-94.5, -30.04) * mm, "construction": true});
            skPoint(sketch, "E134.0", {"position": v(-136, 1.96) * mm});
            skPoint(sketch, "E134.1", {"position": v(-136, -21.04) * mm});
            skLineSegment(sketch, "E135.bottom", {"start": v(-131, -3.04) * mm, "end": v(-141, -3.04) * mm});
            skLineSegment(sketch, "E135.top", {"start": v(-131, 6.96) * mm, "end": v(-141, 6.96) * mm});
            skLineSegment(sketch, "E135.left", {"start": v(-131, -3.04) * mm, "end": v(-131, 6.96) * mm});
            skLineSegment(sketch, "E135.right", {"start": v(-141, -3.04) * mm, "end": v(-141, 6.96) * mm});
            skLineSegment(sketch, "E136.bottom", {"start": v(-131, -26.04) * mm, "end": v(-141, -26.04) * mm});
            skLineSegment(sketch, "E136.top", {"start": v(-131, -16.04) * mm, "end": v(-141, -16.04) * mm});
            skLineSegment(sketch, "E136.left", {"start": v(-131, -26.04) * mm, "end": v(-131, -16.04) * mm});
            skLineSegment(sketch, "E136.right", {"start": v(-141, -26.04) * mm, "end": v(-141, -16.04) * mm});
            skSolve(sketch);
        }
        {
            var Q0;
            Q0=qSketchRegion(id+"F4",true);
            extrude(context, id + "F5", {"entities" : qUnion([Q0]), "operationType" : NewBodyOperationType.REMOVE, "oppositeDirection" : true, "depth" : 5 * mm});
        }
        {
            var Q0;
            Q0=qCreatedBy(makeId("Top.planeOp"),FACE);
            var sketch = newSketch(context, id + "F6", { "sketchPlane" : qUnion([Q0])});
            skLineSegment(sketch, "E137.bottom", {"start": v(-106.79, 77.03) * mm, "end": v(-126.79, 77.03) * mm});
            skLineSegment(sketch, "E137.top", {"start": v(-106.79, 97.03) * mm, "end": v(-126.79, 97.03) * mm});
            skLineSegment(sketch, "E137.left", {"start": v(-106.79, 77.03) * mm, "end": v(-106.79, 97.03) * mm});
            skLineSegment(sketch, "E137.right", {"start": v(-126.79, 77.03) * mm, "end": v(-126.79, 97.03) * mm});
            skPoint(sketch, "E137.middle", {"position": v(-116.79, 87.03) * mm});
            skLineSegment(sketch, "E138.bottom", {"start": v(-105.79, 82.03) * mm, "end": v(-107.79, 82.03) * mm});
            skLineSegment(sketch, "E138.top", {"start": v(-105.79, 92.03) * mm, "end": v(-107.79, 92.03) * mm});
            skLineSegment(sketch, "E138.left", {"start": v(-105.79, 82.03) * mm, "end": v(-105.79, 92.03) * mm});
            skLineSegment(sketch, "E138.right", {"start": v(-107.79, 82.03) * mm, "end": v(-107.79, 92.03) * mm});
            skPoint(sketch, "E138.middle", {"position": v(-106.79, 87.03) * mm});
            skLineSegment(sketch, "E139.bottom", {"start": v(-125.79, 82.03) * mm, "end": v(-127.79, 82.03) * mm});
            skLineSegment(sketch, "E139.top", {"start": v(-125.79, 92.03) * mm, "end": v(-127.79, 92.03) * mm});
            skLineSegment(sketch, "E139.left", {"start": v(-125.79, 82.03) * mm, "end": v(-125.79, 92.03) * mm});
            skLineSegment(sketch, "E139.right", {"start": v(-127.79, 82.03) * mm, "end": v(-127.79, 92.03) * mm});
            skPoint(sketch, "E139.middle", {"position": v(-126.79, 87.03) * mm});
            skLineSegment(sketch, "E140.bottom", {"start": v(-107.79, 78.03) * mm, "end": v(-125.79, 78.03) * mm});
            skLineSegment(sketch, "E140.top", {"start": v(-107.79, 96.03) * mm, "end": v(-125.79, 96.03) * mm});
            skLineSegment(sketch, "E140.left", {"start": v(-107.79, 78.03) * mm, "end": v(-107.79, 96.03) * mm});
            skLineSegment(sketch, "E140.right", {"start": v(-125.79, 78.03) * mm, "end": v(-125.79, 96.03) * mm});
            skLineSegment(sketch, "E141.bottom", {"start": v(-107.79, 86.53) * mm, "end": v(-125.79, 86.53) * mm});
            skLineSegment(sketch, "E141.top", {"start": v(-107.79, 87.53) * mm, "end": v(-125.79, 87.53) * mm});
            skLineSegment(sketch, "E141.left", {"start": v(-107.79, 86.53) * mm, "end": v(-107.79, 87.53) * mm});
            skLineSegment(sketch, "E141.right", {"start": v(-125.79, 86.53) * mm, "end": v(-125.79, 87.53) * mm});
            skLineSegment(sketch, "E142.bottom", {"start": v(-115.79, 85.78) * mm, "end": v(-117.79, 85.78) * mm, "construction": true});
            skLineSegment(sketch, "E142.top", {"start": v(-115.79, 88.28) * mm, "end": v(-117.79, 88.28) * mm, "construction": true});
            skLineSegment(sketch, "E142.left", {"start": v(-115.79, 85.78) * mm, "end": v(-115.79, 88.28) * mm, "construction": true});
            skLineSegment(sketch, "E142.right", {"start": v(-117.79, 85.78) * mm, "end": v(-117.79, 88.28) * mm, "construction": true});
            skLineSegment(sketch, "E143.bottom", {"start": v(-110.82, 38.4) * mm, "end": v(-132.62, 38.4) * mm});
            skLineSegment(sketch, "E143.top", {"start": v(-110.82, 60.2) * mm, "end": v(-132.62, 60.2) * mm});
            skLineSegment(sketch, "E143.left", {"start": v(-110.82, 38.4) * mm, "end": v(-110.82, 60.2) * mm});
            skLineSegment(sketch, "E143.right", {"start": v(-132.62, 38.4) * mm, "end": v(-132.62, 60.2) * mm});
            skPoint(sketch, "E143.middle", {"position": v(-121.72, 49.3) * mm});
            skLineSegment(sketch, "E144.bottom", {"start": v(-110.82, 44.4) * mm, "end": v(-112.62, 44.4) * mm});
            skLineSegment(sketch, "E144.top", {"start": v(-110.82, 54.2) * mm, "end": v(-112.62, 54.2) * mm});
            skLineSegment(sketch, "E144.left", {"start": v(-110.82, 44.4) * mm, "end": v(-110.82, 54.2) * mm});
            skLineSegment(sketch, "E144.right", {"start": v(-112.62, 44.4) * mm, "end": v(-112.62, 54.2) * mm});
            skPoint(sketch, "E144.middle", {"position": v(-111.72, 49.3) * mm});
            skLineSegment(sketch, "E145.bottom", {"start": v(-130.82, 44.4) * mm, "end": v(-132.62, 44.4) * mm});
            skLineSegment(sketch, "E145.top", {"start": v(-130.82, 54.2) * mm, "end": v(-132.62, 54.2) * mm});
            skLineSegment(sketch, "E145.left", {"start": v(-130.82, 44.4) * mm, "end": v(-130.82, 54.2) * mm});
            skLineSegment(sketch, "E145.right", {"start": v(-132.62, 44.4) * mm, "end": v(-132.62, 54.2) * mm});
            skPoint(sketch, "E145.middle", {"position": v(-131.72, 49.3) * mm});
            skLineSegment(sketch, "E146.bottom", {"start": v(-112.62, 40.2) * mm, "end": v(-130.82, 40.2) * mm});
            skLineSegment(sketch, "E146.top", {"start": v(-112.62, 58.4) * mm, "end": v(-130.82, 58.4) * mm});
            skLineSegment(sketch, "E146.left", {"start": v(-112.62, 40.2) * mm, "end": v(-112.62, 58.4) * mm});
            skLineSegment(sketch, "E146.right", {"start": v(-130.82, 40.2) * mm, "end": v(-130.82, 58.4) * mm});
            skSolve(sketch);
        }
        {
            var Q0;
            {var subQ11=sQuery(id+"F6.wireOp",EDGE,"E143.bottom");Q0=makeQuery(id+"F6.imprint","IMPRINT",FACE,{"disambiguationData":[TD([[makeQuery(id+"F6.imprint","IMPRINT",EDGE,{"derivedFrom":subQ11}),-1.0]])]});}
            var Q1;
            {var subQ5=sQuery(id+"F6.wireOp",EDGE,"E144.right");Q1=makeQuery(id+"F6.imprint","IMPRINT",FACE,{"disambiguationData":[TD([[makeQuery(id+"F6.imprint","IMPRINT",EDGE,{"derivedFrom":subQ5}),-1.0]])]});}
            var Q2;
            {var subQ5=sQuery(id+"F6.wireOp",EDGE,"E145.left");Q2=makeQuery(id+"F6.imprint","IMPRINT",FACE,{"disambiguationData":[TD([[makeQuery(id+"F6.imprint","IMPRINT",EDGE,{"derivedFrom":subQ5}),1.0]])]});}
            var Q3;
            {var subQ0=sQuery(id+"F6.wireOp",EDGE,"E145.bottom");Q3=makeQuery(id+"F6.imprint","IMPRINT",FACE,{"disambiguationData":[TD([[makeQuery(id+"F6.imprint","IMPRINT",EDGE,{"derivedFrom":subQ0}),-1.0]])]});}
            var Q4;
            {var subQ2=sQuery(id+"F6.wireOp",EDGE,"E143.top");Q4=makeQuery(id+"F6.imprint","IMPRINT",FACE,{"disambiguationData":[TD([[makeQuery(id+"F6.imprint","IMPRINT",EDGE,{"derivedFrom":subQ2}),1.0]])]});}
            var Q5;
            {var subQ0=sQuery(id+"F6.wireOp",EDGE,"E144.bottom");Q5=makeQuery(id+"F6.imprint","IMPRINT",FACE,{"disambiguationData":[TD([[makeQuery(id+"F6.imprint","IMPRINT",EDGE,{"derivedFrom":subQ0}),-1.0]])]});}
            extrude(context, id + "F7", {"entities" : qUnion([Q0, Q1, Q2, Q3, Q4, Q5]), "depth" : 1 * mm});
        }
        {
            var Q0;
            {var subQ5=sQuery(id+"F6.wireOp",EDGE,"E145.right");Q0=makeQuery(id+"F6.imprint","IMPRINT",FACE,{"disambiguationData":[TD([[makeQuery(id+"F6.imprint","IMPRINT",EDGE,{"derivedFrom":subQ5}),-1.0]])]});}
            var Q1;
            {var subQ5=sQuery(id+"F6.wireOp",EDGE,"E145.left");Q1=makeQuery(id+"F6.imprint","IMPRINT",FACE,{"disambiguationData":[TD([[makeQuery(id+"F6.imprint","IMPRINT",EDGE,{"derivedFrom":subQ5}),1.0]])]});}
            var Q2;
            {var subQ5=sQuery(id+"F6.wireOp",EDGE,"E144.right");Q2=makeQuery(id+"F6.imprint","IMPRINT",FACE,{"disambiguationData":[TD([[makeQuery(id+"F6.imprint","IMPRINT",EDGE,{"derivedFrom":subQ5}),-1.0]])]});}
            var Q3;
            {var subQ5=sQuery(id+"F6.wireOp",EDGE,"E144.left");Q3=makeQuery(id+"F6.imprint","IMPRINT",FACE,{"disambiguationData":[TD([[makeQuery(id+"F6.imprint","IMPRINT",EDGE,{"derivedFrom":subQ5}),1.0]])]});}
            extrude(context, id + "F8", {"entities" : qUnion([Q0, Q1, Q2, Q3]), "operationType" : NewBodyOperationType.ADD, "oppositeDirection" : true, "depth" : 4 * mm});
        }
        {
            var Q0;
            Q0=makeQuery(id+"F7.opExtrude","CAP_FACE",FACE,{"disambiguationData":[OSD([sQuery(id+"F6.wireOp",EDGE,"E143.bottom"),sQuery(id+"F6.wireOp",EDGE,"E143.top"),sQuery(id+"F6.wireOp",EDGE,"E143.left"),sQuery(id+"F6.wireOp",EDGE,"E143.right"),sQuery(id+"F6.wireOp",EDGE,"E144.left"),sQuery(id+"F6.wireOp",EDGE,"E145.right"),sQuery(id+"F6.wireOp",EDGE,"E146.bottom"),sQuery(id+"F6.wireOp",EDGE,"E146.top"),sQuery(id+"F6.wireOp",EDGE,"E146.left"),sQuery(id+"F6.wireOp",EDGE,"E146.right")])],"isStart":false});
            var sketch = newSketch(context, id + "F9", { "sketchPlane" : qUnion([Q0])});
            skPoint(sketch, "E147.0", {"position": v(-121.72, 49.3) * mm});
            skLineSegment(sketch, "E148.bottom", {"start": v(-112.62, 40.2) * mm, "end": v(-130.82, 40.2) * mm});
            skLineSegment(sketch, "E148.top", {"start": v(-112.62, 58.4) * mm, "end": v(-130.82, 58.4) * mm});
            skLineSegment(sketch, "E148.left", {"start": v(-112.62, 40.2) * mm, "end": v(-112.62, 58.4) * mm});
            skLineSegment(sketch, "E148.right", {"start": v(-130.82, 40.2) * mm, "end": v(-130.82, 58.4) * mm});
            skLineSegment(sketch, "E149.0", {"start": v(-131.82, 39.2) * mm, "end": v(-131.82, 59.4) * mm});
            skLineSegment(sketch, "E149.1", {"start": v(-111.62, 39.2) * mm, "end": v(-131.82, 39.2) * mm});
            skLineSegment(sketch, "E149.2", {"start": v(-111.62, 39.2) * mm, "end": v(-111.62, 59.4) * mm});
            skLineSegment(sketch, "E149.3", {"start": v(-111.62, 59.4) * mm, "end": v(-131.82, 59.4) * mm});
            skSolve(sketch);
        }
        {
            var Q0;
            Q0=makeQuery(id+"F9.imprint","IMPRINT",FACE,{"disambiguationData":[TD([[makeQuery(id+"F9.imprint","IMPRINT",EDGE,{"derivedFrom":sQuery(id+"F9.wireOp",EDGE,"E148.bottom")}),1.0]])]});
            extrude(context, id + "F10", {"entities" : qUnion([Q0]), "operationType" : NewBodyOperationType.ADD, "depth" : 5 * mm});
        }
        {
            var Q0;
            Q0=makeQuery(id+"F10.opExtrude","CAP_FACE",FACE,{"disambiguationData":[OSD([sQuery(id+"F9.wireOp",EDGE,"E148.bottom"),sQuery(id+"F9.wireOp",EDGE,"E148.top"),sQuery(id+"F9.wireOp",EDGE,"E148.left"),sQuery(id+"F9.wireOp",EDGE,"E148.right"),sQuery(id+"F9.wireOp",EDGE,"E149.0"),sQuery(id+"F9.wireOp",EDGE,"E149.1"),sQuery(id+"F9.wireOp",EDGE,"E149.2"),sQuery(id+"F9.wireOp",EDGE,"E149.3")])],"isStart":false});
            var sketch = newSketch(context, id + "F11", { "sketchPlane" : qUnion([Q0])});
            skPoint(sketch, "E150.0", {"position": v(-121.72, 49.3) * mm});
            skLineSegment(sketch, "E151.bottom", {"start": v(-112.62, 48.8) * mm, "end": v(-130.82, 48.8) * mm});
            skLineSegment(sketch, "E151.top", {"start": v(-112.62, 49.8) * mm, "end": v(-130.82, 49.8) * mm});
            skLineSegment(sketch, "E151.left", {"start": v(-112.62, 48.8) * mm, "end": v(-112.62, 49.8) * mm});
            skLineSegment(sketch, "E151.right", {"start": v(-130.82, 48.8) * mm, "end": v(-130.82, 49.8) * mm});
            skLineSegment(sketch, "E152.bottom", {"start": v(-121.22, 40.2) * mm, "end": v(-122.22, 40.2) * mm});
            skLineSegment(sketch, "E152.top", {"start": v(-121.22, 58.4) * mm, "end": v(-122.22, 58.4) * mm});
            skLineSegment(sketch, "E152.left", {"start": v(-121.22, 40.2) * mm, "end": v(-121.22, 58.4) * mm});
            skLineSegment(sketch, "E152.right", {"start": v(-122.22, 40.2) * mm, "end": v(-122.22, 58.4) * mm});
            skSolve(sketch);
        }
        {
            var Q0;
            Q0=makeQuery(id+"FvrxBWBR3NFs59h_1.boolean.opBoolean","MERGE",FACE,{"derivedFrom":[makeQuery(id+"F5.boolean.opBoolean","COPY",FACE,{"derivedFrom":makeQuery(id+"F5.opExtrude","CAP_FACE",FACE,{"disambiguationData":[OSD([sQuery(id+"F4.wireOp",EDGE,"E122.bottom"),sQuery(id+"F4.wireOp",EDGE,"E122.top"),sQuery(id+"F4.wireOp",EDGE,"E122.left"),sQuery(id+"F4.wireOp",EDGE,"E122.right")])],"isStart":false})}),makeQuery(id+"FvrxBWBR3NFs59h_1.opExtrude","CAP_FACE",FACE,{"disambiguationData":[OSD([sQuery(id+"FOyiDT4y5zkIJA3_1.wireOp",EDGE,"oN5qgFBu-MPa5-jxRP-8K83-Y7W6XuHjnRPn.bottom"),sQuery(id+"FOyiDT4y5zkIJA3_1.wireOp",EDGE,"oN5qgFBu-MPa5-jxRP-8K83-Y7W6XuHjnRPn.top"),sQuery(id+"FOyiDT4y5zkIJA3_1.wireOp",EDGE,"oN5qgFBu-MPa5-jxRP-8K83-Y7W6XuHjnRPn.left"),sQuery(id+"FOyiDT4y5zkIJA3_1.wireOp",EDGE,"oN5qgFBu-MPa5-jxRP-8K83-Y7W6XuHjnRPn.right")])],"isStart":false}),makeQuery(id+"FvrxBWBR3NFs59h_1.opExtrude","CAP_FACE",FACE,{"disambiguationData":[OSD([sQuery(id+"FOyiDT4y5zkIJA3_1.wireOp",EDGE,"if443p5T-YKs4-1gVt-ORIe-qeo7ftMrQxsQ.bottom"),sQuery(id+"FOyiDT4y5zkIJA3_1.wireOp",EDGE,"if443p5T-YKs4-1gVt-ORIe-qeo7ftMrQxsQ.top"),sQuery(id+"FOyiDT4y5zkIJA3_1.wireOp",EDGE,"if443p5T-YKs4-1gVt-ORIe-qeo7ftMrQxsQ.left"),sQuery(id+"FOyiDT4y5zkIJA3_1.wireOp",EDGE,"if443p5T-YKs4-1gVt-ORIe-qeo7ftMrQxsQ.right")])],"isStart":false})]});
            var sketch = newSketch(context, id + "F12", { "sketchPlane" : qUnion([Q0])});
            skPoint(sketch, "E153.0", {"position": v(-111.5, 1.96) * mm});
            skLineSegment(sketch, "E154.bottom", {"start": v(-108.5, -1.04) * mm, "end": v(-114.5, -1.04) * mm});
            skLineSegment(sketch, "E154.top", {"start": v(-108.5, 4.96) * mm, "end": v(-114.5, 4.96) * mm});
            skLineSegment(sketch, "E154.left", {"start": v(-108.5, -1.04) * mm, "end": v(-108.5, 4.96) * mm});
            skLineSegment(sketch, "E154.right", {"start": v(-114.5, -1.04) * mm, "end": v(-114.5, 4.96) * mm});
            skSolve(sketch);
        }
        {
            var Q0;
            {var subQ0=sQuery(id+"F12.wireOp",EDGE,"E154.top");Q0=makeQuery(id+"F12.imprint","IMPRINT",FACE,{"disambiguationData":[TD([[makeQuery(id+"F12.imprint","IMPRINT",EDGE,{"derivedFrom":subQ0}),1.0]])]});}
            var Q1;
            {var subQ0=sQuery(id+"F12.wireOp",EDGE,"E154.left");var subQ1=makeQuery(id+"F5.opExtrude","CAP_FACE",FACE,{"disambiguationData":[OSD([sQuery(id+"F4.wireOp",EDGE,"E122.bottom"),sQuery(id+"F4.wireOp",EDGE,"E122.top"),sQuery(id+"F4.wireOp",EDGE,"E122.left"),sQuery(id+"F4.wireOp",EDGE,"E122.right")])],"isStart":false});var subQ2=sQuery(id+"F0.wireOp",EDGE,"E33.trimOffspring");var subQ3=makeQuery(id+"F5.boolean.opBoolean","INTERSECT",EDGE,{"derivedFrom":[makeQuery(id+"F3.boolean.opBoolean","MERGE",FACE,{"derivedFrom":[makeQuery(id+"F2.opExtrude","SWEPT_FACE",FACE,{"disambiguationData":[OSD([subQ2])]}),makeQuery(id+"F3.opExtrude","SWEPT_FACE",FACE,{"disambiguationData":[OSD([subQ2])]})]}),subQ1]});var subQ4=makeQuery(id+"F12.imprint","INTERSECT",VERTEX,{"derivedFrom":[subQ3,subQ0]});Q1=makeQuery(id+"F12.imprint","IMPRINT",FACE,{"disambiguationData":[TD([[makeQuery(id+"F12.imprint","IMPRINT",EDGE,{"disambiguationData":[TD([[subQ4,-1.0]])],"derivedFrom":subQ0}),1.0]])]});}
            var Q2;
            {var subQ0=sQuery(id+"F12.wireOp",EDGE,"E154.bottom");Q2=makeQuery(id+"F12.imprint","IMPRINT",FACE,{"disambiguationData":[TD([[makeQuery(id+"F12.imprint","IMPRINT",EDGE,{"derivedFrom":subQ0}),-1.0]])]});}
            extrude(context, id + "F13", {"entities" : qUnion([Q0, Q1, Q2]), "operationType" : NewBodyOperationType.ADD, "depth" : 8 * mm});
        }
        {
            var Q0;
            Q0=qSketchRegion(id+"F11",true);
            extrude(context, id + "F14", {"entities" : qUnion([Q0]), "operationType" : NewBodyOperationType.ADD, "oppositeDirection" : true, "depth" : 6 * mm});
        }
        {
            var Q0;
            Q0=makeQuery(id+"F14.boolean.opBoolean","MERGE",FACE,{"derivedFrom":[makeQuery(id+"F10.opExtrude","CAP_FACE",FACE,{"disambiguationData":[OSD([sQuery(id+"F9.wireOp",EDGE,"E148.bottom"),sQuery(id+"F9.wireOp",EDGE,"E148.top"),sQuery(id+"F9.wireOp",EDGE,"E148.left"),sQuery(id+"F9.wireOp",EDGE,"E148.right"),sQuery(id+"F9.wireOp",EDGE,"E149.0"),sQuery(id+"F9.wireOp",EDGE,"E149.1"),sQuery(id+"F9.wireOp",EDGE,"E149.2"),sQuery(id+"F9.wireOp",EDGE,"E149.3")])],"isStart":false}),makeQuery(id+"F14.opExtrude","CAP_FACE",FACE,{"disambiguationData":[OSD([sQuery(id+"F11.wireOp",EDGE,"E151.bottom"),sQuery(id+"F11.wireOp",EDGE,"E151.top"),sQuery(id+"F11.wireOp",EDGE,"E151.left"),sQuery(id+"F11.wireOp",EDGE,"E151.right"),sQuery(id+"F11.wireOp",EDGE,"E152.bottom"),sQuery(id+"F11.wireOp",EDGE,"E152.top"),sQuery(id+"F11.wireOp",EDGE,"E152.left"),sQuery(id+"F11.wireOp",EDGE,"E152.right")])],"isStart":true})]});
            var sketch = newSketch(context, id + "F15", { "sketchPlane" : qUnion([Q0])});
            skPoint(sketch, "E155.0", {"position": v(-130.82, 58.4) * mm});
            skPoint(sketch, "E155.1", {"position": v(-112.62, 40.2) * mm});
            skLineSegment(sketch, "E156.bottom", {"start": v(-130.82, 58.4) * mm, "end": v(-112.62, 58.4) * mm});
            skLineSegment(sketch, "E156.top", {"start": v(-130.82, 40.2) * mm, "end": v(-112.62, 40.2) * mm});
            skLineSegment(sketch, "E156.left", {"start": v(-130.82, 58.4) * mm, "end": v(-130.82, 40.2) * mm});
            skLineSegment(sketch, "E156.right", {"start": v(-112.62, 58.4) * mm, "end": v(-112.62, 40.2) * mm});
            skSolve(sketch);
        }
        {
            var Q0;
            Q0=qSketchRegion(id+"F15",true);
            extrude(context, id + "F16", {"entities" : qUnion([Q0]), "operationType" : NewBodyOperationType.REMOVE, "oppositeDirection" : true, "depth" : 1 * mm});
        }
        {
            var Q0;
            {var subQ0=sQuery(id+"F6.wireOp",EDGE,"E145.right");var subQ2=sQuery(id+"F6.wireOp",EDGE,"E146.right");var subQ4=sQuery(id+"F6.wireOp",EDGE,"E144.left");var subQ6=sQuery(id+"F6.wireOp",EDGE,"E146.left");var subQ8=sQuery(id+"F6.wireOp",EDGE,"E143.top");var subQ9=sQuery(id+"F6.wireOp",EDGE,"E143.left");var subQ11=sQuery(id+"F6.wireOp",EDGE,"E143.right");var subQ13=sQuery(id+"F6.wireOp",EDGE,"E146.top");var subQ16=sQuery(id+"F6.wireOp",EDGE,"E146.bottom");var subQ17=sQuery(id+"F6.wireOp",EDGE,"E143.bottom");var subQ18=makeQuery(id+"F7.opExtrude","CAP_FACE",FACE,{"disambiguationData":[OSD([subQ17,subQ8,subQ9,subQ11,subQ4,subQ0,subQ16,subQ13,subQ6,subQ2])],"isStart":true});Q0=makeQuery(id+"F14.boolean.opBoolean","MERGE",FACE,{"derivedFrom":[makeQuery(id+"F8.boolean.opBoolean","SPLIT",FACE,{"disambiguationData":[TD([makeQuery(id+"F7.opExtrude","SWEPT_FACE",FACE,{"disambiguationData":[OSD([subQ17])]})])],"derivedFrom":subQ18}),makeQuery(id+"F8.boolean.opBoolean","SPLIT",FACE,{"disambiguationData":[TD([makeQuery(id+"F7.opExtrude","SWEPT_FACE",FACE,{"disambiguationData":[OSD([subQ8])]})])],"derivedFrom":subQ18}),makeQuery(id+"F14.opExtrude","CAP_FACE",FACE,{"disambiguationData":[OSD([sQuery(id+"F11.wireOp",EDGE,"E151.bottom"),sQuery(id+"F11.wireOp",EDGE,"E151.top"),sQuery(id+"F11.wireOp",EDGE,"E151.left"),sQuery(id+"F11.wireOp",EDGE,"E151.right"),sQuery(id+"F11.wireOp",EDGE,"E152.bottom"),sQuery(id+"F11.wireOp",EDGE,"E152.top"),sQuery(id+"F11.wireOp",EDGE,"E152.left"),sQuery(id+"F11.wireOp",EDGE,"E152.right")])],"isStart":false})]});}
            var sketch = newSketch(context, id + "F17", { "sketchPlane" : qUnion([Q0])});
            skPoint(sketch, "E157.0", {"position": v(-121.72, -40.2) * mm});
            skLineSegment(sketch, "E158.bottom", {"start": v(-120.72, -50.54) * mm, "end": v(-122.72, -50.54) * mm});
            skLineSegment(sketch, "E158.top", {"start": v(-120.72, -48.04) * mm, "end": v(-122.72, -48.04) * mm});
            skLineSegment(sketch, "E158.left", {"start": v(-120.72, -50.54) * mm, "end": v(-120.72, -48.04) * mm});
            skLineSegment(sketch, "E158.right", {"start": v(-122.72, -50.54) * mm, "end": v(-122.72, -48.04) * mm});
            skPoint(sketch, "E158.middle", {"position": v(-121.72, -49.3) * mm});
            skPoint(sketch, "E158.middle.positionSnap0", {"position": v(-130.82, -49.3) * mm});
            skPoint(sketch, "E158.centerSnap0", {"position": v(-130.82, -49.3) * mm});
            skSolve(sketch);
        }
        {
            var Q0;
            Q0=makeQuery(id+"F13.opExtrude","CAP_FACE",FACE,{"disambiguationData":[OSD([sQuery(id+"F12.wireOp",EDGE,"E154.bottom"),sQuery(id+"F12.wireOp",EDGE,"E154.top"),sQuery(id+"F12.wireOp",EDGE,"E154.left"),sQuery(id+"F12.wireOp",EDGE,"E154.right")])],"isStart":false});
            var sketch = newSketch(context, id + "F18", { "sketchPlane" : qUnion([Q0])});
            skPoint(sketch, "E159.0", {"position": v(-111.5, 1.96) * mm});
            skLineSegment(sketch, "E160.bottom", {"start": v(-110.5, 0.7) * mm, "end": v(-112.5, 0.7) * mm});
            skLineSegment(sketch, "E160.top", {"start": v(-110.5, 3.2) * mm, "end": v(-112.5, 3.2) * mm});
            skLineSegment(sketch, "E160.left", {"start": v(-110.5, 0.7) * mm, "end": v(-110.5, 3.2) * mm});
            skLineSegment(sketch, "E160.right", {"start": v(-112.5, 0.7) * mm, "end": v(-112.5, 3.2) * mm});
            skSolve(sketch);
        }
        {
            var Q0;
            Q0=qSketchRegion(id+"F18",true);
            extrude(context, id + "F19", {"entities" : qUnion([Q0]), "operationType" : NewBodyOperationType.ADD, "depth" : 2 * mm});
        }
        {
            var Q0;
            {var subQ0=sQuery(id+"F11.wireOp",EDGE,"E151.right");var subQ1=sQuery(id+"F11.wireOp",EDGE,"E151.bottom");var subQ4=sQuery(id+"F11.wireOp",EDGE,"E152.right");var subQ5=sQuery(id+"F6.wireOp",EDGE,"E146.right");var subQ8=sQuery(id+"F11.wireOp",EDGE,"E151.top");var subQ9=sQuery(id+"F6.wireOp",EDGE,"E145.right");var subQ11=sQuery(id+"F6.wireOp",EDGE,"E144.left");var subQ13=sQuery(id+"F6.wireOp",EDGE,"E146.left");var subQ15=sQuery(id+"F6.wireOp",EDGE,"E143.top");var subQ16=sQuery(id+"F6.wireOp",EDGE,"E143.left");var subQ18=sQuery(id+"F6.wireOp",EDGE,"E143.right");var subQ20=sQuery(id+"F6.wireOp",EDGE,"E146.top");var subQ22=sQuery(id+"F6.wireOp",EDGE,"E146.bottom");var subQ23=sQuery(id+"F6.wireOp",EDGE,"E143.bottom");var subQ24=makeQuery(id+"F7.opExtrude","CAP_FACE",FACE,{"disambiguationData":[OSD([subQ23,subQ15,subQ16,subQ18,subQ11,subQ9,subQ22,subQ20,subQ13,subQ5])],"isStart":true});Q0=makeQuery(id+"F22.boolean.opBoolean","SPLIT",FACE,{"disambiguationData":[TD([makeQuery(id+"F22.opExtrude","SWEPT_FACE",FACE,{"disambiguationData":[OSD([sQuery(id+"F17.wireOp",EDGE,"E158.right")])]})])],"derivedFrom":makeQuery(id+"F14.boolean.opBoolean","MERGE",FACE,{"derivedFrom":[makeQuery(id+"F8.boolean.opBoolean","SPLIT",FACE,{"disambiguationData":[TD([makeQuery(id+"F7.opExtrude","SWEPT_FACE",FACE,{"disambiguationData":[OSD([subQ23])]})])],"derivedFrom":subQ24}),makeQuery(id+"F8.boolean.opBoolean","SPLIT",FACE,{"disambiguationData":[TD([makeQuery(id+"F7.opExtrude","SWEPT_FACE",FACE,{"disambiguationData":[OSD([subQ15])]})])],"derivedFrom":subQ24}),makeQuery(id+"F14.opExtrude","CAP_FACE",FACE,{"disambiguationData":[OSD([subQ1,subQ8,sQuery(id+"F11.wireOp",EDGE,"E151.left"),subQ0,sQuery(id+"F11.wireOp",EDGE,"E152.bottom"),sQuery(id+"F11.wireOp",EDGE,"E152.top"),sQuery(id+"F11.wireOp",EDGE,"E152.left"),subQ4])],"isStart":false})]})});}
            var sketch = newSketch(context, id + "F20", { "sketchPlane" : qUnion([Q0])});
            skPoint(sketch, "E161.0", {"position": v(-126.52, -48.8) * mm});
            skPoint(sketch, "E162.0", {"position": v(-122.22, -44.5) * mm});
            skPoint(sketch, "E163.0", {"position": v(-122.22, -40.2) * mm});
            skLineSegment(sketch, "E164.bottom", {"start": v(-122.22, -40.2) * mm, "end": v(-130.82, -40.2) * mm});
            skLineSegment(sketch, "E164.top", {"start": v(-122.22, -48.8) * mm, "end": v(-130.82, -48.8) * mm});
            skLineSegment(sketch, "E164.left", {"start": v(-122.22, -40.2) * mm, "end": v(-122.22, -48.8) * mm});
            skLineSegment(sketch, "E164.right", {"start": v(-130.82, -40.2) * mm, "end": v(-130.82, -48.8) * mm});
            skPoint(sketch, "E164.middle", {"position": v(-126.52, -44.5) * mm});
            skLineSegment(sketch, "E165.bottom", {"start": v(-122.72, -40.7) * mm, "end": v(-130.32, -40.7) * mm});
            skLineSegment(sketch, "E165.top", {"start": v(-122.72, -48.3) * mm, "end": v(-130.32, -48.3) * mm});
            skLineSegment(sketch, "E165.left", {"start": v(-122.72, -40.7) * mm, "end": v(-122.72, -48.3) * mm});
            skLineSegment(sketch, "E165.right", {"start": v(-130.32, -40.7) * mm, "end": v(-130.32, -48.3) * mm});
            skLineSegment(sketch, "E166.direction1", {"start": v(-130.82, -48.8) * mm, "end": v(-121.22, -48.8) * mm, "construction": true});
            skLineSegment(sketch, "E167.0.1.0", {"start": v(-113.12, -40.7) * mm, "end": v(-120.72, -40.7) * mm});
            skLineSegment(sketch, "E167.3.1.0", {"start": v(-112.62, -40.2) * mm, "end": v(-121.22, -40.2) * mm});
            skLineSegment(sketch, "E167.6.1.0", {"start": v(-112.62, -48.8) * mm, "end": v(-121.22, -48.8) * mm});
            skLineSegment(sketch, "E167.9.1.0", {"start": v(-112.62, -40.2) * mm, "end": v(-112.62, -48.8) * mm});
            skPoint(sketch, "E167.12.1.0", {"position": v(-116.92, -44.5) * mm});
            skLineSegment(sketch, "E167.13.1.0", {"start": v(-113.12, -40.7) * mm, "end": v(-113.12, -48.3) * mm});
            skLineSegment(sketch, "E167.16.1.0", {"start": v(-120.72, -40.7) * mm, "end": v(-120.72, -48.3) * mm});
            skLineSegment(sketch, "E167.19.1.0", {"start": v(-121.22, -40.2) * mm, "end": v(-121.22, -48.8) * mm});
            skPoint(sketch, "E167.22.1.0", {"position": v(-112.62, -44.5) * mm});
            skPoint(sketch, "E167.23.1.0", {"position": v(-112.62, -40.2) * mm});
            skLineSegment(sketch, "E167.24.1.0", {"start": v(-113.12, -48.3) * mm, "end": v(-120.72, -48.3) * mm});
            skPoint(sketch, "E167.27.1.0", {"position": v(-116.92, -48.8) * mm});
            skPoint(sketch, "E167.28.1.0", {"position": v(-116.92, -44.5) * mm});
            skSolve(sketch);
        }
        {
            var Q0;
            Q0=qSketchRegion(id+"F20",true);
            extrude(context, id + "F21", {"entities" : qUnion([Q0]), "operationType" : NewBodyOperationType.ADD, "oppositeDirection" : true, "depth" : 2 * mm});
        }
        {
            var Q0;
            Q0=qSketchRegion(id+"F17",true);
            extrude(context, id + "F22", {"entities" : qUnion([Q0]), "operationType" : NewBodyOperationType.REMOVE, "oppositeDirection" : true, "depth" : 2 * mm});
        }
        {
            var Q0;
            Q0=makeQuery(id+"F0.imprint","IMPRINT",FACE,{"disambiguationData":[TD([[makeQuery(id+"F0.imprint","IMPRINT",EDGE,{"derivedFrom":sQuery(id+"F0.wireOp",EDGE,"E0.bottom")}),-1.0]])]});
            var sketch = newSketch(context, id + "F23", { "sketchPlane" : qUnion([Q0])});
            skLineSegment(sketch, "E168.top", {"start": v(-145.5, -33.04) * mm, "end": v(-44.5, -33.04) * mm});
            skLineSegment(sketch, "E168.left", {"start": v(-145.5, -55.04) * mm, "end": v(-145.5, -33.04) * mm});
            skLineSegment(sketch, "E169.top", {"start": v(-31.5, -11.04) * mm, "end": v(-44.5, -11.04) * mm});
            skLineSegment(sketch, "E169.right", {"start": v(-44.5, -33.04) * mm, "end": v(-44.5, -11.04) * mm});
            skLineSegment(sketch, "E170.top", {"start": v(-15.5, 11.96) * mm, "end": v(-31.5, 11.96) * mm});
            skLineSegment(sketch, "E170.right", {"start": v(-31.5, -11.04) * mm, "end": v(-31.5, 11.96) * mm});
            skLineSegment(sketch, "E171", {"start": v(-15.5, 11.96) * mm, "end": v(-15.5, -55.04) * mm});
            skLineSegment(sketch, "E172", {"start": v(-145.5, -55.04) * mm, "end": v(-15.5, -55.04) * mm});
            skLineSegment(sketch, "E173.bottom", {"start": v(-44.5, -33.04) * mm, "end": v(-15.5, -33.04) * mm});
            skLineSegment(sketch, "E173.top", {"start": v(-44.5, -31.04) * mm, "end": v(-15.5, -31.04) * mm});
            skLineSegment(sketch, "E173.left", {"start": v(-44.5, -33.04) * mm, "end": v(-44.5, -31.04) * mm});
            skLineSegment(sketch, "E173.right", {"start": v(-15.5, -33.04) * mm, "end": v(-15.5, -31.04) * mm});
            skLineSegment(sketch, "E174.bottom", {"start": v(-31.5, -11.04) * mm, "end": v(-15.5, -11.04) * mm});
            skLineSegment(sketch, "E174.top", {"start": v(-31.5, -9.04) * mm, "end": v(-15.5, -9.04) * mm});
            skLineSegment(sketch, "E174.left", {"start": v(-31.5, -11.04) * mm, "end": v(-31.5, -9.04) * mm});
            skLineSegment(sketch, "E174.right", {"start": v(-15.5, -11.04) * mm, "end": v(-15.5, -9.04) * mm});
            skSolve(sketch);
        }
        {
            var Q0;
            Q0=makeQuery(id+"F23.imprint","IMPRINT",FACE,{"disambiguationData":[TD([[makeQuery(id+"F23.imprint","IMPRINT",EDGE,{"derivedFrom":makeQuery(id+"F0.imprint","IMPRINT",EDGE,{"derivedFrom":sQuery(id+"F0.wireOp",EDGE,"E5")})}),1.0]])]});
            var Q1;
            Q1=makeQuery(id+"F23.imprint","IMPRINT",FACE,{"disambiguationData":[TD([[makeQuery(id+"F23.imprint","IMPRINT",EDGE,{"derivedFrom":makeQuery(id+"F0.imprint","IMPRINT",EDGE,{"derivedFrom":sQuery(id+"F0.wireOp",EDGE,"E6")})}),1.0]])]});
            var Q2;
            Q2=makeQuery(id+"F23.imprint","IMPRINT",FACE,{"disambiguationData":[TD([[makeQuery(id+"F23.imprint","IMPRINT",EDGE,{"derivedFrom":makeQuery(id+"F0.imprint","IMPRINT",EDGE,{"derivedFrom":sQuery(id+"F0.wireOp",EDGE,"E7")})}),1.0]])]});
            var Q3;
            Q3=makeQuery(id+"F23.imprint","IMPRINT",FACE,{"disambiguationData":[TD([[makeQuery(id+"F23.imprint","IMPRINT",EDGE,{"derivedFrom":makeQuery(id+"F0.imprint","IMPRINT",EDGE,{"derivedFrom":sQuery(id+"F0.wireOp",EDGE,"E10")})}),1.0]])]});
            var Q4;
            Q4=makeQuery(id+"F23.imprint","IMPRINT",FACE,{"disambiguationData":[TD([[makeQuery(id+"F23.imprint","IMPRINT",EDGE,{"derivedFrom":makeQuery(id+"F0.imprint","IMPRINT",EDGE,{"derivedFrom":sQuery(id+"F0.wireOp",EDGE,"E11")})}),1.0]])]});
            var Q5;
            Q5=makeQuery(id+"F23.imprint","IMPRINT",FACE,{"disambiguationData":[TD([[makeQuery(id+"F23.imprint","IMPRINT",EDGE,{"derivedFrom":makeQuery(id+"F0.imprint","IMPRINT",EDGE,{"derivedFrom":sQuery(id+"F0.wireOp",EDGE,"E12")})}),1.0]])]});
            var Q6;
            Q6=makeQuery(id+"F23.imprint","IMPRINT",FACE,{"disambiguationData":[TD([[makeQuery(id+"F23.imprint","IMPRINT",EDGE,{"derivedFrom":makeQuery(id+"F0.imprint","IMPRINT",EDGE,{"derivedFrom":sQuery(id+"F0.wireOp",EDGE,"E13")})}),1.0]])]});
            var Q7;
            Q7=makeQuery(id+"F23.imprint","IMPRINT",FACE,{"disambiguationData":[TD([[makeQuery(id+"F23.imprint","IMPRINT",EDGE,{"derivedFrom":makeQuery(id+"F0.imprint","IMPRINT",EDGE,{"derivedFrom":sQuery(id+"F0.wireOp",EDGE,"E14")})}),1.0]])]});
            var Q8;
            Q8=makeQuery(id+"F23.imprint","IMPRINT",FACE,{"disambiguationData":[TD([[makeQuery(id+"F23.imprint","IMPRINT",EDGE,{"derivedFrom":makeQuery(id+"F0.imprint","IMPRINT",EDGE,{"derivedFrom":sQuery(id+"F0.wireOp",EDGE,"E15")})}),1.0]])]});
            var Q9;
            Q9=makeQuery(id+"F23.imprint","IMPRINT",FACE,{"disambiguationData":[TD([[makeQuery(id+"F23.imprint","IMPRINT",EDGE,{"derivedFrom":makeQuery(id+"F0.imprint","IMPRINT",EDGE,{"derivedFrom":sQuery(id+"F0.wireOp",EDGE,"E16")})}),1.0]])]});
            var Q10;
            Q10=makeQuery(id+"F23.imprint","IMPRINT",FACE,{"disambiguationData":[TD([[makeQuery(id+"F23.imprint","IMPRINT",EDGE,{"derivedFrom":makeQuery(id+"F0.imprint","IMPRINT",EDGE,{"derivedFrom":sQuery(id+"F0.wireOp",EDGE,"E18")})}),1.0]])]});
            var Q11;
            Q11=makeQuery(id+"F23.imprint","IMPRINT",FACE,{"disambiguationData":[TD([[makeQuery(id+"F23.imprint","IMPRINT",EDGE,{"derivedFrom":makeQuery(id+"F0.imprint","IMPRINT",EDGE,{"derivedFrom":sQuery(id+"F0.wireOp",EDGE,"E19")})}),1.0]])]});
            var Q12;
            {var subQ1=sQuery(id+"F23.wireOp",EDGE,"E170.top");Q12=makeQuery(id+"F23.imprint","IMPRINT",FACE,{"disambiguationData":[TD([[makeQuery(id+"F23.imprint","IMPRINT",EDGE,{"derivedFrom":subQ1}),1.0]])]});}
            var Q13;
            Q13=makeQuery(id+"F23.imprint","IMPRINT",FACE,{"disambiguationData":[TD([[makeQuery(id+"F23.imprint","IMPRINT",EDGE,{"derivedFrom":sQuery(id+"F23.wireOp",EDGE,"E169.top")}),1.0]])]});
            var Q14;
            Q14=makeQuery(id+"F23.imprint","IMPRINT",FACE,{"disambiguationData":[TD([[makeQuery(id+"F23.imprint","IMPRINT",EDGE,{"derivedFrom":sQuery(id+"F23.wireOp",EDGE,"E168.top")}),-1.0]])]});
            extrude(context, id + "F24", {"entities" : qUnion([Q0, Q1, Q2, Q3, Q4, Q5, Q6, Q7, Q8, Q9, Q10, Q11, Q12, Q13, Q14]), "operationType" : NewBodyOperationType.REMOVE, "depth" : 5 * mm});
        }
        {
            var Q0;
            Q0=makeQuery(id+"F1.imprint","IMPRINT",FACE,{"disambiguationData":[TD([[makeQuery(id+"F1.imprint","IMPRINT",EDGE,{"derivedFrom":sQuery(id+"F1.wireOp",EDGE,"E56.bottom")}),-1.0]])]});
            var Q1;
            {var subQ0=sQuery(id+"F1.wireOp",EDGE,"E107.right");var subQ1=sQuery(id+"F1.wireOp",EDGE,"E107.top");var subQ2=makeQuery(id+"F1.imprint","INTERSECT",VERTEX,{"derivedFrom":[subQ1,subQ0]});Q1=makeQuery(id+"F1.imprint","IMPRINT",FACE,{"disambiguationData":[TD([[makeQuery(id+"F1.imprint","IMPRINT",EDGE,{"disambiguationData":[TD([[subQ2,1.0]])],"derivedFrom":subQ1}),1.0]])]});}
            var Q2;
            {var subQ0=sQuery(id+"F1.wireOp",EDGE,"E107.left");var subQ1=sQuery(id+"F1.wireOp",EDGE,"E107.top");var subQ2=makeQuery(id+"F1.imprint","INTERSECT",VERTEX,{"derivedFrom":[subQ1,subQ0]});Q2=makeQuery(id+"F1.imprint","IMPRINT",FACE,{"disambiguationData":[TD([[makeQuery(id+"F1.imprint","IMPRINT",EDGE,{"disambiguationData":[TD([[subQ2,-1.0]])],"derivedFrom":subQ1}),1.0]])]});}
            var Q3;
            {var subQ0=sQuery(id+"F1.wireOp",EDGE,"E107.right");var subQ1=sQuery(id+"F1.wireOp",EDGE,"E107.bottom");var subQ2=makeQuery(id+"F1.imprint","INTERSECT",VERTEX,{"derivedFrom":[subQ1,subQ0]});Q3=makeQuery(id+"F1.imprint","IMPRINT",FACE,{"disambiguationData":[TD([[makeQuery(id+"F1.imprint","IMPRINT",EDGE,{"disambiguationData":[TD([[subQ2,1.0]])],"derivedFrom":subQ1}),-1.0]])]});}
            var Q4;
            {var subQ0=sQuery(id+"F1.wireOp",EDGE,"E107.left");var subQ1=sQuery(id+"F1.wireOp",EDGE,"E107.bottom");var subQ2=makeQuery(id+"F1.imprint","INTERSECT",VERTEX,{"derivedFrom":[subQ1,subQ0]});Q4=makeQuery(id+"F1.imprint","IMPRINT",FACE,{"disambiguationData":[TD([[makeQuery(id+"F1.imprint","IMPRINT",EDGE,{"disambiguationData":[TD([[subQ2,-1.0]])],"derivedFrom":subQ1}),-1.0]])]});}
            var Q5;
            {var subQ0=sQuery(id+"F1.wireOp",EDGE,"E106.right");var subQ1=sQuery(id+"F1.wireOp",EDGE,"E106.top");var subQ2=makeQuery(id+"F1.imprint","INTERSECT",VERTEX,{"derivedFrom":[subQ1,subQ0]});Q5=makeQuery(id+"F1.imprint","IMPRINT",FACE,{"disambiguationData":[TD([[makeQuery(id+"F1.imprint","IMPRINT",EDGE,{"disambiguationData":[TD([[subQ2,1.0]])],"derivedFrom":subQ1}),1.0]])]});}
            var Q6;
            {var subQ0=sQuery(id+"F1.wireOp",EDGE,"E106.left");var subQ1=sQuery(id+"F1.wireOp",EDGE,"E106.top");var subQ2=makeQuery(id+"F1.imprint","INTERSECT",VERTEX,{"derivedFrom":[subQ1,subQ0]});Q6=makeQuery(id+"F1.imprint","IMPRINT",FACE,{"disambiguationData":[TD([[makeQuery(id+"F1.imprint","IMPRINT",EDGE,{"disambiguationData":[TD([[subQ2,-1.0]])],"derivedFrom":subQ1}),1.0]])]});}
            var Q7;
            {var subQ0=sQuery(id+"F1.wireOp",EDGE,"E106.right");var subQ1=sQuery(id+"F1.wireOp",EDGE,"E106.bottom");var subQ2=makeQuery(id+"F1.imprint","INTERSECT",VERTEX,{"derivedFrom":[subQ1,subQ0]});Q7=makeQuery(id+"F1.imprint","IMPRINT",FACE,{"disambiguationData":[TD([[makeQuery(id+"F1.imprint","IMPRINT",EDGE,{"disambiguationData":[TD([[subQ2,1.0]])],"derivedFrom":subQ1}),-1.0]])]});}
            var Q8;
            {var subQ0=sQuery(id+"F1.wireOp",EDGE,"E106.left");var subQ1=sQuery(id+"F1.wireOp",EDGE,"E106.bottom");var subQ2=makeQuery(id+"F1.imprint","INTERSECT",VERTEX,{"derivedFrom":[subQ1,subQ0]});Q8=makeQuery(id+"F1.imprint","IMPRINT",FACE,{"disambiguationData":[TD([[makeQuery(id+"F1.imprint","IMPRINT",EDGE,{"disambiguationData":[TD([[subQ2,-1.0]])],"derivedFrom":subQ1}),-1.0]])]});}
            extrude(context, id + "F25", {"entities" : qUnion([Q0, Q1, Q2, Q3, Q4, Q5, Q6, Q7, Q8]), "depth" : 2 * mm});
        }
        {
            var Q0;
            Q0=makeQuery(id+"F3.opExtrude","CAP_FACE",FACE,{"disambiguationData":[OSD([sQuery(id+"F0.wireOp",EDGE,"E0.bottom"),sQuery(id+"F0.wireOp",EDGE,"E0.top"),sQuery(id+"F0.wireOp",EDGE,"E0.left"),sQuery(id+"F0.wireOp",EDGE,"E0.right"),sQuery(id+"F0.wireOp",EDGE,"E5"),sQuery(id+"F0.wireOp",EDGE,"E6"),sQuery(id+"F0.wireOp",EDGE,"E7"),sQuery(id+"F0.wireOp",EDGE,"E10"),sQuery(id+"F0.wireOp",EDGE,"E11"),sQuery(id+"F0.wireOp",EDGE,"E12"),sQuery(id+"F0.wireOp",EDGE,"E13"),sQuery(id+"F0.wireOp",EDGE,"E14"),sQuery(id+"F0.wireOp",EDGE,"E15"),sQuery(id+"F0.wireOp",EDGE,"E16"),sQuery(id+"F0.wireOp",EDGE,"E17.bottom"),sQuery(id+"F0.wireOp",EDGE,"E17.top"),sQuery(id+"F0.wireOp",EDGE,"E17.left"),sQuery(id+"F0.wireOp",EDGE,"E17.right"),sQuery(id+"F0.wireOp",EDGE,"E18"),sQuery(id+"F0.wireOp",EDGE,"E19"),sQuery(id+"F0.wireOp",EDGE,"E21.bottom"),sQuery(id+"F0.wireOp",EDGE,"E21.top"),sQuery(id+"F0.wireOp",EDGE,"E21.left"),sQuery(id+"F0.wireOp",EDGE,"E21.right"),sQuery(id+"F0.wireOp",EDGE,"E23.bottom"),sQuery(id+"F0.wireOp",EDGE,"E23.top"),sQuery(id+"F0.wireOp",EDGE,"E24.left"),sQuery(id+"F0.wireOp",EDGE,"E24.right"),sQuery(id+"F0.wireOp",EDGE,"E25.left"),sQuery(id+"F0.wireOp",EDGE,"E25.right"),sQuery(id+"F0.wireOp",EDGE,"E26.trimOffspring"),sQuery(id+"F0.wireOp",EDGE,"E27.trimOffspring"),sQuery(id+"F0.wireOp",EDGE,"E28.trimOffspring"),sQuery(id+"F0.wireOp",EDGE,"E29.trimOffspring"),sQuery(id+"F0.wireOp",EDGE,"E30.trimOffspring"),sQuery(id+"F0.wireOp",EDGE,"E31.trimOffspring"),sQuery(id+"F0.wireOp",EDGE,"E32.trimOffspring"),sQuery(id+"F0.wireOp",EDGE,"E33.trimOffspring"),sQuery(id+"F0.wireOp",EDGE,"E22.bottom"),sQuery(id+"F0.wireOp",EDGE,"E22.top"),sQuery(id+"F0.wireOp",EDGE,"E22.left"),sQuery(id+"F0.wireOp",EDGE,"E22.right"),sQuery(id+"F0.wireOp",EDGE,"E35.bottom"),sQuery(id+"F0.wireOp",EDGE,"E35.top"),sQuery(id+"F0.wireOp",EDGE,"E36.left"),sQuery(id+"F0.wireOp",EDGE,"E36.right"),sQuery(id+"F0.wireOp",EDGE,"E37.left"),sQuery(id+"F0.wireOp",EDGE,"E37.right"),sQuery(id+"F0.wireOp",EDGE,"E38.trimOffspring"),sQuery(id+"F0.wireOp",EDGE,"E39.trimOffspring"),sQuery(id+"F0.wireOp",EDGE,"E40.trimOffspring"),sQuery(id+"F0.wireOp",EDGE,"E41.trimOffspring"),sQuery(id+"F0.wireOp",EDGE,"E42.trimOffspring"),sQuery(id+"F0.wireOp",EDGE,"E43.trimOffspring"),sQuery(id+"F0.wireOp",EDGE,"E44.trimOffspring"),sQuery(id+"F0.wireOp",EDGE,"E45.trimOffspring"),sQuery(id+"F0.wireOp",EDGE,"E46.bottom"),sQuery(id+"F0.wireOp",EDGE,"E46.top"),sQuery(id+"F0.wireOp",EDGE,"E46.left"),sQuery(id+"F0.wireOp",EDGE,"E46.right"),sQuery(id+"F0.wireOp",EDGE,"E47.bottom"),sQuery(id+"F0.wireOp",EDGE,"E47.top"),sQuery(id+"F0.wireOp",EDGE,"E47.left"),sQuery(id+"F0.wireOp",EDGE,"E47.right"),sQuery(id+"F0.wireOp",EDGE,"E48.1.0.0"),sQuery(id+"F0.wireOp",EDGE,"E48.1.0.2"),sQuery(id+"F0.wireOp",EDGE,"E48.1.0.3"),sQuery(id+"F0.wireOp",EDGE,"E48.1.0.5"),sQuery(id+"F0.wireOp",EDGE,"E48.1.0.6"),sQuery(id+"F0.wireOp",EDGE,"E48.1.0.7"),sQuery(id+"F0.wireOp",EDGE,"E48.1.0.8"),sQuery(id+"F0.wireOp",EDGE,"E48.1.0.9"),sQuery(id+"F0.wireOp",EDGE,"E48.1.0.12"),sQuery(id+"F0.wireOp",EDGE,"E48.1.0.13"),sQuery(id+"F0.wireOp",EDGE,"E48.1.0.14"),sQuery(id+"F0.wireOp",EDGE,"E48.1.0.15"),sQuery(id+"F0.wireOp",EDGE,"E48.1.0.16"),sQuery(id+"F0.wireOp",EDGE,"E48.1.0.17"),sQuery(id+"F0.wireOp",EDGE,"E48.1.0.18"),sQuery(id+"F0.wireOp",EDGE,"E48.1.0.19"),sQuery(id+"F0.wireOp",EDGE,"E48.1.0.20"),sQuery(id+"F0.wireOp",EDGE,"E48.1.0.21"),sQuery(id+"F0.wireOp",EDGE,"E48.2.0.0"),sQuery(id+"F0.wireOp",EDGE,"E48.2.0.2"),sQuery(id+"F0.wireOp",EDGE,"E48.2.0.3"),sQuery(id+"F0.wireOp",EDGE,"E48.2.0.5"),sQuery(id+"F0.wireOp",EDGE,"E48.2.0.6"),sQuery(id+"F0.wireOp",EDGE,"E48.2.0.7"),sQuery(id+"F0.wireOp",EDGE,"E48.2.0.8"),sQuery(id+"F0.wireOp",EDGE,"E48.2.0.9"),sQuery(id+"F0.wireOp",EDGE,"E48.2.0.12"),sQuery(id+"F0.wireOp",EDGE,"E48.2.0.13"),sQuery(id+"F0.wireOp",EDGE,"E48.2.0.14"),sQuery(id+"F0.wireOp",EDGE,"E48.2.0.15"),sQuery(id+"F0.wireOp",EDGE,"E48.2.0.16"),sQuery(id+"F0.wireOp",EDGE,"E48.2.0.17"),sQuery(id+"F0.wireOp",EDGE,"E48.2.0.18"),sQuery(id+"F0.wireOp",EDGE,"E48.2.0.19"),sQuery(id+"F0.wireOp",EDGE,"E48.2.0.20"),sQuery(id+"F0.wireOp",EDGE,"E48.2.0.21"),sQuery(id+"F0.wireOp",EDGE,"E49.1.0.0"),sQuery(id+"F0.wireOp",EDGE,"E49.1.0.1"),sQuery(id+"F0.wireOp",EDGE,"E49.1.0.2"),sQuery(id+"F0.wireOp",EDGE,"E49.1.0.4"),sQuery(id+"F0.wireOp",EDGE,"E49.1.0.6"),sQuery(id+"F0.wireOp",EDGE,"E49.1.0.7"),sQuery(id+"F0.wireOp",EDGE,"E49.1.0.9"),sQuery(id+"F0.wireOp",EDGE,"E49.1.0.10"),sQuery(id+"F0.wireOp",EDGE,"E49.1.0.12"),sQuery(id+"F0.wireOp",EDGE,"E49.1.0.14"),sQuery(id+"F0.wireOp",EDGE,"E49.1.0.16"),sQuery(id+"F0.wireOp",EDGE,"E49.1.0.18"),sQuery(id+"F0.wireOp",EDGE,"E49.1.0.19"),sQuery(id+"F0.wireOp",EDGE,"E49.1.0.20"),sQuery(id+"F0.wireOp",EDGE,"E49.1.0.26"),sQuery(id+"F0.wireOp",EDGE,"E49.1.0.28"),sQuery(id+"F0.wireOp",EDGE,"E49.1.0.29"),sQuery(id+"F0.wireOp",EDGE,"E49.1.0.30"),sQuery(id+"F0.wireOp",EDGE,"E49.2.0.0"),sQuery(id+"F0.wireOp",EDGE,"E49.2.0.1"),sQuery(id+"F0.wireOp",EDGE,"E49.2.0.2"),sQuery(id+"F0.wireOp",EDGE,"E49.2.0.4"),sQuery(id+"F0.wireOp",EDGE,"E49.2.0.6"),sQuery(id+"F0.wireOp",EDGE,"E49.2.0.7"),sQuery(id+"F0.wireOp",EDGE,"E49.2.0.9"),sQuery(id+"F0.wireOp",EDGE,"E49.2.0.10"),sQuery(id+"F0.wireOp",EDGE,"E49.2.0.12"),sQuery(id+"F0.wireOp",EDGE,"E49.2.0.14"),sQuery(id+"F0.wireOp",EDGE,"E49.2.0.16"),sQuery(id+"F0.wireOp",EDGE,"E49.2.0.18"),sQuery(id+"F0.wireOp",EDGE,"E49.2.0.19"),sQuery(id+"F0.wireOp",EDGE,"E49.2.0.20"),sQuery(id+"F0.wireOp",EDGE,"E49.2.0.26"),sQuery(id+"F0.wireOp",EDGE,"E49.2.0.28"),sQuery(id+"F0.wireOp",EDGE,"E49.2.0.29"),sQuery(id+"F0.wireOp",EDGE,"E49.2.0.30"),sQuery(id+"F0.wireOp",EDGE,"E50.left"),sQuery(id+"F0.wireOp",EDGE,"E50.right"),sQuery(id+"F0.wireOp",EDGE,"E51.left"),sQuery(id+"F0.wireOp",EDGE,"E51.right"),sQuery(id+"F0.wireOp",EDGE,"E52"),sQuery(id+"F0.wireOp",EDGE,"E53"),sQuery(id+"F0.wireOp",EDGE,"E54"),sQuery(id+"F0.wireOp",EDGE,"E55")])],"isStart":false});
            var sketch = newSketch(context, id + "F26", { "sketchPlane" : qUnion([Q0])});
            skLineSegment(sketch, "E175.bottom", {"start": v(-155.5, 17.96) * mm, "end": v(-145.5, 17.96) * mm});
            skLineSegment(sketch, "E175.top", {"start": v(-155.5, -57.04) * mm, "end": v(-145.5, -57.04) * mm});
            skLineSegment(sketch, "E175.left", {"start": v(-155.5, 17.96) * mm, "end": v(-155.5, -57.04) * mm});
            skLineSegment(sketch, "E175.right", {"start": v(-145.5, 17.96) * mm, "end": v(-145.5, -57.04) * mm});
            skLineSegment(sketch, "E176.bottom", {"start": v(-5.5, -57.04) * mm, "end": v(-15.5, -57.04) * mm});
            skLineSegment(sketch, "E176.top", {"start": v(-5.5, 17.96) * mm, "end": v(-15.5, 17.96) * mm});
            skLineSegment(sketch, "E176.left", {"start": v(-5.5, -57.04) * mm, "end": v(-5.5, 17.96) * mm});
            skLineSegment(sketch, "E176.right", {"start": v(-15.5, -57.04) * mm, "end": v(-15.5, 17.96) * mm});
            skSolve(sketch);
        }
        {
            var Q0;
            Q0=makeQuery(id+"F26.imprint","IMPRINT",FACE,{"disambiguationData":[TD([[makeQuery(id+"F26.imprint","IMPRINT",EDGE,{"derivedFrom":sQuery(id+"F26.wireOp",EDGE,"E176.bottom")}),-1.0]])]});
            var Q1;
            Q1=makeQuery(id+"F26.imprint","IMPRINT",FACE,{"disambiguationData":[TD([[makeQuery(id+"F26.imprint","IMPRINT",EDGE,{"derivedFrom":sQuery(id+"F26.wireOp",EDGE,"E175.bottom")}),1.0]])]});
            extrude(context, id + "F27", {"entities" : qUnion([Q0, Q1]), "operationType" : NewBodyOperationType.ADD, "depth" : 4 * mm});
        }
        {
            var Q0;
            {var subQ0=sQuery(id+"F0.wireOp",EDGE,"E0.bottom");Q0=makeQuery(id+"F27.boolean.opBoolean","MERGE",FACE,{"derivedFrom":[makeQuery(id+"FcxvOkpkAmDw7ie_3.boolean.opBoolean","MERGE",FACE,{"derivedFrom":[makeQuery(id+"F3.boolean.opBoolean","MERGE",FACE,{"derivedFrom":[makeQuery(id+"F2.opExtrude","SWEPT_FACE",FACE,{"disambiguationData":[OSD([subQ0])]}),makeQuery(id+"F3.opExtrude","SWEPT_FACE",FACE,{"disambiguationData":[OSD([subQ0])]})]}),makeQuery(id+"FcxvOkpkAmDw7ie_3.opExtrude","SWEPT_FACE",FACE,{"disambiguationData":[OSD([sQuery(id+"FNICA6uDXxchBR6_3.wireOp",EDGE,"OznuT0um-5Ypx-SHlm-bkf4-iYFOqL2Sfz4i.bottom")])]})]}),makeQuery(id+"F27.opExtrude","SWEPT_FACE",FACE,{"disambiguationData":[OSD([sQuery(id+"F26.wireOp",EDGE,"E175.top")])]}),makeQuery(id+"F27.opExtrude","SWEPT_FACE",FACE,{"disambiguationData":[OSD([sQuery(id+"F26.wireOp",EDGE,"E176.bottom")])]})]});}
            var sketch = newSketch(context, id + "F28", { "sketchPlane" : qUnion([Q0])});
            skLineSegment(sketch, "E177.bottom", {"start": v(-155.5, 0) * mm, "end": v(-147.5, 0) * mm});
            skLineSegment(sketch, "E177.top", {"start": v(-155.5, 7) * mm, "end": v(-147.5, 7) * mm});
            skLineSegment(sketch, "E177.left", {"start": v(-155.5, 0) * mm, "end": v(-155.5, 7) * mm});
            skLineSegment(sketch, "E177.right", {"start": v(-147.5, 0) * mm, "end": v(-147.5, 7) * mm});
            skLineSegment(sketch, "E178.bottom", {"start": v(-5.5, 0) * mm, "end": v(-13.5, 0) * mm});
            skLineSegment(sketch, "E178.top", {"start": v(-5.5, 7) * mm, "end": v(-13.5, 7) * mm});
            skLineSegment(sketch, "E178.left", {"start": v(-5.5, 0) * mm, "end": v(-5.5, 7) * mm});
            skLineSegment(sketch, "E178.right", {"start": v(-13.5, 0) * mm, "end": v(-13.5, 7) * mm});
            skSolve(sketch);
        }
        {
            var Q0;
            Q0=qSketchRegion(id+"F28",true);
            extrude(context, id + "F29", {"entities" : qUnion([Q0]), "operationType" : NewBodyOperationType.REMOVE, "oppositeDirection" : true, "depth" : 77.8 * mm});
        }
        {
            var Q0;
            {var subQ0=sQuery(id+"F0.wireOp",EDGE,"E0.right");var subQ1=sQuery(id+"F0.wireOp",EDGE,"E0.top");var subQ3=sQuery(id+"F0.wireOp",EDGE,"E0.bottom");var subQ5=sQuery(id+"F0.wireOp",EDGE,"E53");var subQ6=sQuery(id+"F0.wireOp",EDGE,"E52");var subQ7=sQuery(id+"F0.wireOp",EDGE,"E51.right");var subQ8=sQuery(id+"F0.wireOp",EDGE,"E51.left");var subQ9=sQuery(id+"F0.wireOp",EDGE,"E50.right");var subQ10=sQuery(id+"F0.wireOp",EDGE,"E50.left");var subQ11=sQuery(id+"F0.wireOp",EDGE,"E49.2.0.30");var subQ12=sQuery(id+"F0.wireOp",EDGE,"E49.2.0.0");var subQ13=sQuery(id+"F0.wireOp",EDGE,"E49.2.0.29");var subQ16=sQuery(id+"F0.wireOp",EDGE,"E49.2.0.10");var subQ17=sQuery(id+"F0.wireOp",EDGE,"E49.2.0.28");var subQ20=sQuery(id+"F0.wireOp",EDGE,"E49.2.0.18");var subQ21=sQuery(id+"F0.wireOp",EDGE,"E49.2.0.26");var subQ24=sQuery(id+"F0.wireOp",EDGE,"E49.2.0.1");var subQ25=sQuery(id+"F0.wireOp",EDGE,"E49.2.0.19");var subQ27=sQuery(id+"F0.wireOp",EDGE,"E49.2.0.9");var subQ30=sQuery(id+"F0.wireOp",EDGE,"E49.2.0.4");var subQ34=sQuery(id+"F0.wireOp",EDGE,"E49.2.0.2");var subQ35=sQuery(id+"F0.wireOp",EDGE,"E49.2.0.7");var subQ37=sQuery(id+"F0.wireOp",EDGE,"E49.2.0.16");var subQ39=sQuery(id+"F0.wireOp",EDGE,"E49.2.0.20");var subQ41=sQuery(id+"F0.wireOp",EDGE,"E49.2.0.12");var subQ43=sQuery(id+"F0.wireOp",EDGE,"E49.2.0.14");var subQ44=sQuery(id+"F0.wireOp",EDGE,"E49.2.0.6");var subQ45=sQuery(id+"F0.wireOp",EDGE,"E49.1.0.30");var subQ46=sQuery(id+"F0.wireOp",EDGE,"E49.1.0.0");var subQ47=sQuery(id+"F0.wireOp",EDGE,"E49.1.0.29");var subQ50=sQuery(id+"F0.wireOp",EDGE,"E49.1.0.10");var subQ51=sQuery(id+"F0.wireOp",EDGE,"E49.1.0.28");var subQ54=sQuery(id+"F0.wireOp",EDGE,"E49.1.0.18");var subQ55=sQuery(id+"F0.wireOp",EDGE,"E49.1.0.26");var subQ58=sQuery(id+"F0.wireOp",EDGE,"E49.1.0.1");var subQ59=sQuery(id+"F0.wireOp",EDGE,"E49.1.0.19");var subQ61=sQuery(id+"F0.wireOp",EDGE,"E49.1.0.9");var subQ64=sQuery(id+"F0.wireOp",EDGE,"E49.1.0.4");var subQ68=sQuery(id+"F0.wireOp",EDGE,"E49.1.0.2");var subQ69=sQuery(id+"F0.wireOp",EDGE,"E49.1.0.7");var subQ71=sQuery(id+"F0.wireOp",EDGE,"E49.1.0.16");var subQ73=sQuery(id+"F0.wireOp",EDGE,"E49.1.0.20");var subQ75=sQuery(id+"F0.wireOp",EDGE,"E49.1.0.12");var subQ77=sQuery(id+"F0.wireOp",EDGE,"E49.1.0.14");var subQ78=sQuery(id+"F0.wireOp",EDGE,"E49.1.0.6");var subQ79=sQuery(id+"F0.wireOp",EDGE,"E48.2.0.21");var subQ81=sQuery(id+"F0.wireOp",EDGE,"E48.2.0.20");var subQ82=sQuery(id+"F0.wireOp",EDGE,"E48.2.0.12");var subQ83=sQuery(id+"F0.wireOp",EDGE,"E48.2.0.15");var subQ86=sQuery(id+"F0.wireOp",EDGE,"E48.2.0.13");var subQ87=sQuery(id+"F0.wireOp",EDGE,"E48.2.0.17");var subQ90=sQuery(id+"F0.wireOp",EDGE,"E48.2.0.19");var subQ91=sQuery(id+"F0.wireOp",EDGE,"E48.2.0.18");var subQ93=sQuery(id+"F0.wireOp",EDGE,"E48.2.0.16");var subQ97=sQuery(id+"F0.wireOp",EDGE,"E48.2.0.2");var subQ99=sQuery(id+"F0.wireOp",EDGE,"E48.2.0.3");var subQ102=sQuery(id+"F0.wireOp",EDGE,"E48.2.0.0");var subQ104=sQuery(id+"F0.wireOp",EDGE,"E48.2.0.5");var subQ105=sQuery(id+"F0.wireOp",EDGE,"E48.2.0.14");var subQ108=sQuery(id+"F0.wireOp",EDGE,"E48.2.0.6");var subQ110=sQuery(id+"F0.wireOp",EDGE,"E48.2.0.9");var subQ111=sQuery(id+"F0.wireOp",EDGE,"E48.2.0.8");var subQ112=sQuery(id+"F0.wireOp",EDGE,"E48.2.0.7");var subQ113=sQuery(id+"F0.wireOp",EDGE,"E37.left");var subQ114=sQuery(id+"F0.wireOp",EDGE,"E36.right");var subQ115=sQuery(id+"F0.wireOp",EDGE,"E36.left");var subQ116=sQuery(id+"F0.wireOp",EDGE,"E35.top");var subQ117=sQuery(id+"F0.wireOp",EDGE,"E35.bottom");var subQ118=sQuery(id+"F0.wireOp",EDGE,"E22.right");var subQ119=sQuery(id+"F0.wireOp",EDGE,"E22.top");var subQ121=sQuery(id+"F0.wireOp",EDGE,"E39.trimOffspring");var subQ124=sQuery(id+"F0.wireOp",EDGE,"E22.bottom");var subQ126=sQuery(id+"F0.wireOp",EDGE,"E41.trimOffspring");var subQ128=sQuery(id+"F0.wireOp",EDGE,"E22.left");var subQ132=sQuery(id+"F0.wireOp",EDGE,"E38.trimOffspring");var subQ135=sQuery(id+"F0.wireOp",EDGE,"E30.trimOffspring");var subQ136=sQuery(id+"F0.wireOp",EDGE,"E44.trimOffspring");var subQ139=sQuery(id+"F0.wireOp",EDGE,"E29.trimOffspring");var subQ142=sQuery(id+"F0.wireOp",EDGE,"E27.trimOffspring");var subQ146=sQuery(id+"F0.wireOp",EDGE,"E26.trimOffspring");var subQ147=sQuery(id+"F0.wireOp",EDGE,"E33.trimOffspring");var subQ148=sQuery(id+"F0.wireOp",EDGE,"E25.right");var subQ149=sQuery(id+"F0.wireOp",EDGE,"E32.trimOffspring");var subQ150=sQuery(id+"F0.wireOp",EDGE,"E25.left");var subQ151=sQuery(id+"F0.wireOp",EDGE,"E31.trimOffspring");var subQ152=sQuery(id+"F0.wireOp",EDGE,"E24.right");var subQ153=sQuery(id+"F0.wireOp",EDGE,"E24.left");var subQ154=sQuery(id+"F0.wireOp",EDGE,"E23.top");var subQ155=sQuery(id+"F0.wireOp",EDGE,"E28.trimOffspring");var subQ156=sQuery(id+"F0.wireOp",EDGE,"E23.bottom");var subQ157=sQuery(id+"F0.wireOp",EDGE,"E21.right");var subQ158=sQuery(id+"F0.wireOp",EDGE,"E21.top");var subQ162=sQuery(id+"F0.wireOp",EDGE,"E21.bottom");var subQ165=sQuery(id+"F0.wireOp",EDGE,"E17.top");var subQ168=sQuery(id+"F0.wireOp",EDGE,"E17.bottom");var subQ171=sQuery(id+"F0.wireOp",EDGE,"E37.right");var subQ174=sQuery(id+"F0.wireOp",EDGE,"E48.1.0.16");var subQ175=sQuery(id+"F0.wireOp",EDGE,"E17.right");var subQ176=sQuery(id+"F0.wireOp",EDGE,"E17.left");var subQ177=sQuery(id+"F0.wireOp",EDGE,"E21.left");var subQ180=sQuery(id+"F0.wireOp",EDGE,"E40.trimOffspring");var subQ181=sQuery(id+"F0.wireOp",EDGE,"E42.trimOffspring");var subQ185=sQuery(id+"F0.wireOp",EDGE,"E48.1.0.17");var subQ186=sQuery(id+"F0.wireOp",EDGE,"E48.1.0.20");var subQ193=sQuery(id+"F0.wireOp",EDGE,"E48.1.0.19");var subQ200=sQuery(id+"F0.wireOp",EDGE,"E43.trimOffspring");var subQ201=sQuery(id+"F0.wireOp",EDGE,"E45.trimOffspring");var subQ202=sQuery(id+"F0.wireOp",EDGE,"E46.left");var subQ203=sQuery(id+"F0.wireOp",EDGE,"E46.bottom");var subQ206=sQuery(id+"F0.wireOp",EDGE,"E46.right");var subQ208=sQuery(id+"F0.wireOp",EDGE,"E46.top");var subQ212=sQuery(id+"F0.wireOp",EDGE,"E47.left");var subQ213=sQuery(id+"F0.wireOp",EDGE,"E47.bottom");var subQ216=sQuery(id+"F0.wireOp",EDGE,"E47.right");var subQ218=sQuery(id+"F0.wireOp",EDGE,"E47.top");var subQ222=sQuery(id+"F0.wireOp",EDGE,"E48.1.0.0");var subQ223=sQuery(id+"F0.wireOp",EDGE,"E48.1.0.2");var subQ226=sQuery(id+"F0.wireOp",EDGE,"E48.1.0.9");var subQ228=sQuery(id+"F0.wireOp",EDGE,"E48.1.0.15");var subQ230=sQuery(id+"F0.wireOp",EDGE,"E48.1.0.8");var subQ232=sQuery(id+"F0.wireOp",EDGE,"E48.1.0.3");var subQ233=sQuery(id+"F0.wireOp",EDGE,"E48.1.0.5");var subQ234=sQuery(id+"F0.wireOp",EDGE,"E48.1.0.6");var subQ235=sQuery(id+"F0.wireOp",EDGE,"E48.1.0.7");var subQ236=sQuery(id+"F0.wireOp",EDGE,"E48.1.0.12");var subQ237=sQuery(id+"F0.wireOp",EDGE,"E48.1.0.13");var subQ238=sQuery(id+"F0.wireOp",EDGE,"E48.1.0.14");var subQ246=sQuery(id+"F0.wireOp",EDGE,"E48.1.0.18");var subQ251=sQuery(id+"F0.wireOp",EDGE,"E48.1.0.21");var subQ255=sQuery(id+"F0.wireOp",EDGE,"E55");var subQ256=sQuery(id+"F0.wireOp",EDGE,"E54");var subQ257=sQuery(id+"F0.wireOp",EDGE,"E0.left");var subQ258=makeQuery(id+"F2.opExtrude","CAP_FACE",FACE,{"disambiguationData":[OSD([subQ3,subQ1,subQ257,subQ0,sQuery(id+"F0.wireOp",EDGE,"E5"),sQuery(id+"F0.wireOp",EDGE,"E6"),sQuery(id+"F0.wireOp",EDGE,"E7"),sQuery(id+"F0.wireOp",EDGE,"E10"),sQuery(id+"F0.wireOp",EDGE,"E11"),sQuery(id+"F0.wireOp",EDGE,"E12"),sQuery(id+"F0.wireOp",EDGE,"E13"),sQuery(id+"F0.wireOp",EDGE,"E14"),sQuery(id+"F0.wireOp",EDGE,"E15"),sQuery(id+"F0.wireOp",EDGE,"E16"),subQ168,subQ165,subQ176,subQ175,sQuery(id+"F0.wireOp",EDGE,"E18"),sQuery(id+"F0.wireOp",EDGE,"E19"),subQ162,subQ158,subQ177,subQ157,subQ156,subQ154,subQ153,subQ152,subQ150,subQ148,subQ146,subQ142,subQ155,subQ139,subQ135,subQ151,subQ149,subQ147,subQ124,subQ119,subQ128,subQ118,subQ117,subQ116,subQ115,subQ114,subQ113,subQ171,subQ132,subQ121,subQ180,subQ126,subQ181,subQ200,subQ136,subQ201,subQ203,subQ208,subQ202,subQ206,subQ213,subQ218,subQ212,subQ216,subQ222,subQ223,subQ232,subQ233,subQ234,subQ235,subQ230,subQ226,subQ236,subQ237,subQ238,subQ228,subQ174,subQ185,subQ246,subQ193,subQ186,subQ251,subQ102,subQ97,subQ99,subQ104,subQ108,subQ112,subQ111,subQ110,subQ82,subQ86,subQ105,subQ83,subQ93,subQ87,subQ91,subQ90,subQ81,subQ79,subQ46,subQ58,subQ68,subQ64,subQ78,subQ69,subQ61,subQ50,subQ75,subQ77,subQ71,subQ54,subQ59,subQ73,subQ55,subQ51,subQ47,subQ45,subQ12,subQ24,subQ34,subQ30,subQ44,subQ35,subQ27,subQ16,subQ41,subQ43,subQ37,subQ20,subQ25,subQ39,subQ21,subQ17,subQ13,subQ11,subQ10,subQ9,subQ8,subQ7,subQ6,subQ5,subQ256,subQ255])],"isStart":true});Q0=makeQuery(id+"FcxvOkpkAmDw7ie_3.boolean.opBoolean","MERGE",FACE,{"derivedFrom":[makeQuery(id+"F24.boolean.opBoolean","SPLIT",FACE,{"disambiguationData":[TD([makeQuery(id+"F2.opExtrude","SWEPT_FACE",FACE,{"disambiguationData":[OSD([subQ257])]})])],"derivedFrom":subQ258}),makeQuery(id+"F24.boolean.opBoolean","SPLIT",FACE,{"disambiguationData":[TD([makeQuery(id+"F2.opExtrude","SWEPT_FACE",FACE,{"disambiguationData":[OSD([subQ0])]})])],"derivedFrom":subQ258}),makeQuery(id+"FcxvOkpkAmDw7ie_3.opExtrude","CAP_FACE",FACE,{"disambiguationData":[OSD([sQuery(id+"FNICA6uDXxchBR6_3.wireOp",EDGE,"OznuT0um-5Ypx-SHlm-bkf4-iYFOqL2Sfz4i.bottom"),sQuery(id+"FNICA6uDXxchBR6_3.wireOp",EDGE,"OznuT0um-5Ypx-SHlm-bkf4-iYFOqL2Sfz4i.top"),sQuery(id+"FNICA6uDXxchBR6_3.wireOp",EDGE,"OznuT0um-5Ypx-SHlm-bkf4-iYFOqL2Sfz4i.left"),sQuery(id+"FNICA6uDXxchBR6_3.wireOp",EDGE,"OznuT0um-5Ypx-SHlm-bkf4-iYFOqL2Sfz4i.right")])],"isStart":false}),makeQuery(id+"FcxvOkpkAmDw7ie_3.opExtrude","CAP_FACE",FACE,{"disambiguationData":[OSD([sQuery(id+"FNICA6uDXxchBR6_3.wireOp",EDGE,"YSd4T3NJ-1L5Y-MwVD-52kg-DvB7oUMf2wlW.bottom"),sQuery(id+"FNICA6uDXxchBR6_3.wireOp",EDGE,"YSd4T3NJ-1L5Y-MwVD-52kg-DvB7oUMf2wlW.top"),sQuery(id+"FNICA6uDXxchBR6_3.wireOp",EDGE,"YSd4T3NJ-1L5Y-MwVD-52kg-DvB7oUMf2wlW.left"),sQuery(id+"FNICA6uDXxchBR6_3.wireOp",EDGE,"YSd4T3NJ-1L5Y-MwVD-52kg-DvB7oUMf2wlW.right")])],"isStart":false}),makeQuery(id+"FcxvOkpkAmDw7ie_3.opExtrude","CAP_FACE",FACE,{"disambiguationData":[OSD([sQuery(id+"FNICA6uDXxchBR6_3.wireOp",EDGE,"awoJ12up-LfxG-riiH-PCTd-TFvWrLSTyvKZ.bottom"),sQuery(id+"FNICA6uDXxchBR6_3.wireOp",EDGE,"awoJ12up-LfxG-riiH-PCTd-TFvWrLSTyvKZ.top"),sQuery(id+"FNICA6uDXxchBR6_3.wireOp",EDGE,"awoJ12up-LfxG-riiH-PCTd-TFvWrLSTyvKZ.left"),sQuery(id+"FNICA6uDXxchBR6_3.wireOp",EDGE,"awoJ12up-LfxG-riiH-PCTd-TFvWrLSTyvKZ.right")])],"isStart":false}),makeQuery(id+"FcxvOkpkAmDw7ie_3.opExtrude","CAP_FACE",FACE,{"disambiguationData":[OSD([sQuery(id+"FNICA6uDXxchBR6_3.wireOp",EDGE,"WfW6qyGR-5Y5B-en90-Dwp4-fLCMDk8WttTC.bottom"),sQuery(id+"FNICA6uDXxchBR6_3.wireOp",EDGE,"WfW6qyGR-5Y5B-en90-Dwp4-fLCMDk8WttTC.top"),sQuery(id+"FNICA6uDXxchBR6_3.wireOp",EDGE,"WfW6qyGR-5Y5B-en90-Dwp4-fLCMDk8WttTC.left"),sQuery(id+"FNICA6uDXxchBR6_3.wireOp",EDGE,"WfW6qyGR-5Y5B-en90-Dwp4-fLCMDk8WttTC.right")])],"isStart":false})]});}
            var sketch = newSketch(context, id + "F30", { "sketchPlane" : qUnion([Q0])});
            skLineSegment(sketch, "E179.bottom", {"start": v(-147.5, -17.96) * mm, "end": v(-13.5, -17.96) * mm});
            skLineSegment(sketch, "E179.top", {"start": v(-147.5, -15.46) * mm, "end": v(-13.5, -15.46) * mm});
            skLineSegment(sketch, "E179.left", {"start": v(-147.5, -17.96) * mm, "end": v(-147.5, -15.46) * mm});
            skLineSegment(sketch, "E179.right", {"start": v(-13.5, -17.96) * mm, "end": v(-13.5, -15.46) * mm});
            skSolve(sketch);
        }
        {
            var Q0;
            Q0=qSketchRegion(id+"F30",true);
            extrude(context, id + "F31", {"entities" : qUnion([Q0]), "operationType" : NewBodyOperationType.REMOVE, "oppositeDirection" : true, "depth" : 3 * mm});
        }
    });
